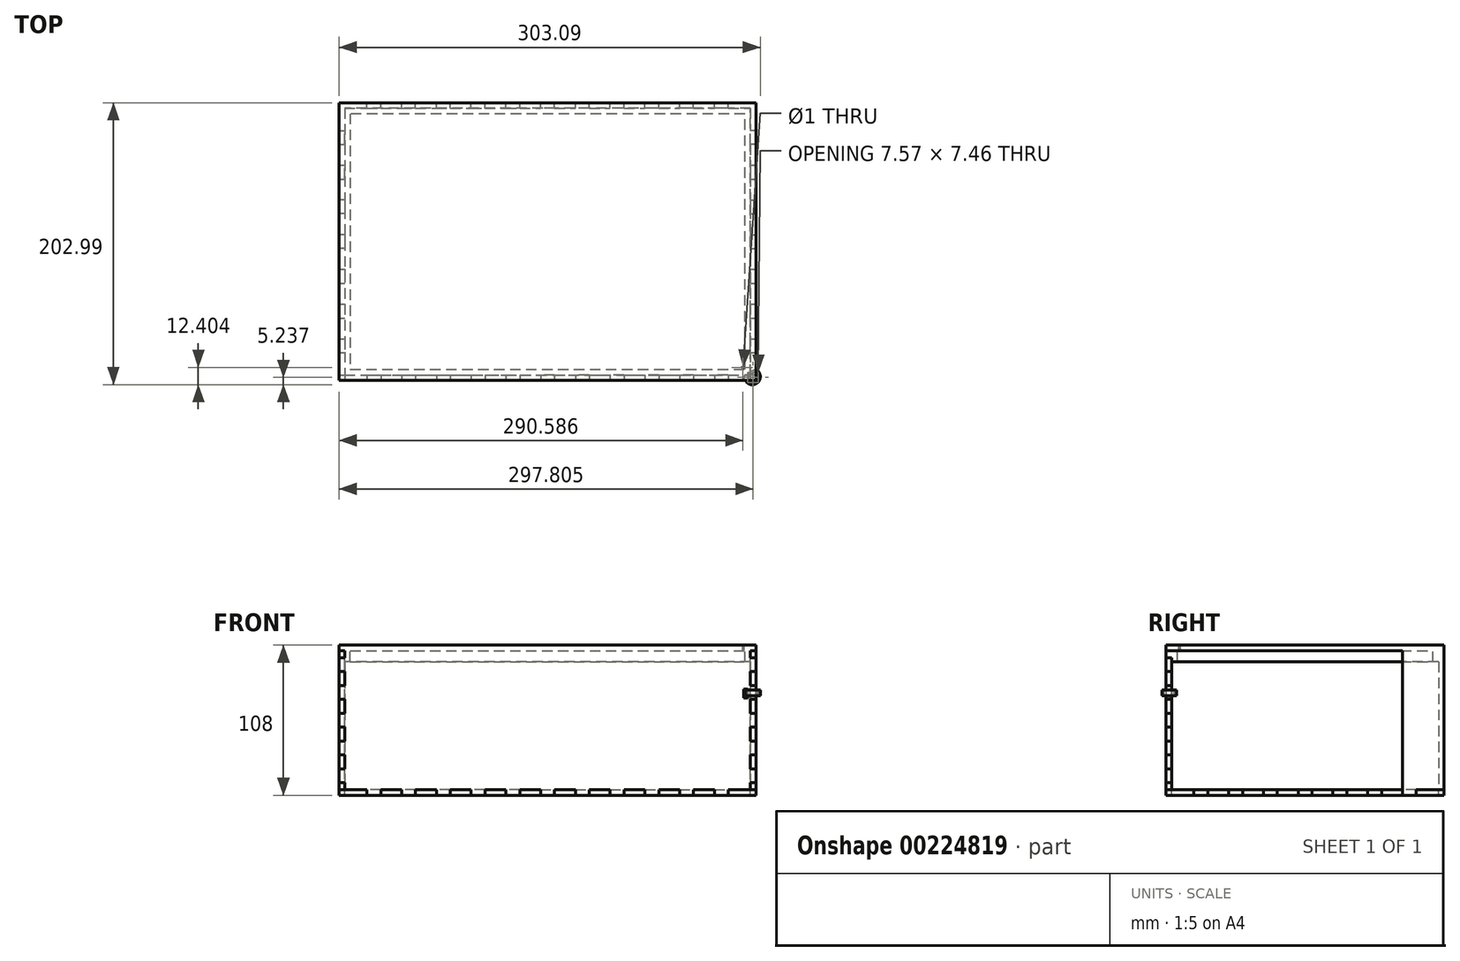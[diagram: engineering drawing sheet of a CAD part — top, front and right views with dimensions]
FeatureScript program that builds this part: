
annotation { "Feature Type Name" : "Feature", "Feature Type Description" : "" }
export const myFeature = defineFeature(function(context is Context, id is Id, definition is map)
    precondition{}
    {
        {
            var Q0;
            Q0=qCreatedBy(makeId("Top.planeOp"),FACE);
            var sketch = newSketch(context, id + "F0", { "sketchPlane" : qUnion([Q0])});
            skPoint(sketch, "E0.middle", {"position": v(0, 0) * mm});
            skLineSegment(sketch, "E1", {"start": v(-150, 0) * mm, "end": v(-150, 0) * mm, "construction": true});
            skPoint(sketch, "E1.endSnap0", {"position": v(-150, 0) * mm});
            skLineSegment(sketch, "E2", {"start": v(-146, 5) * mm, "end": v(-150, 5) * mm});
            skLineSegment(sketch, "E3.MirrorCS", {"start": v(-146, -5) * mm, "end": v(-150, -5) * mm});
            skLineSegment(sketch, "E4", {"start": v(-146, 5) * mm, "end": v(-146, -5) * mm});
            skLineSegment(sketch, "E5", {"start": v(-150, 0) * mm, "end": v(-83.06, 0) * mm, "construction": true});
            skLineSegment(sketch, "E6.0.1.0", {"start": v(-146, 30) * mm, "end": v(-150, 30) * mm});
            skLineSegment(sketch, "E6.0.1.1", {"start": v(-146, 30) * mm, "end": v(-146, 20) * mm});
            skLineSegment(sketch, "E6.0.1.2", {"start": v(-146, 20) * mm, "end": v(-150, 20) * mm});
            skLineSegment(sketch, "E6.0.2.0", {"start": v(-146, 55) * mm, "end": v(-150, 55) * mm});
            skLineSegment(sketch, "E6.0.2.1", {"start": v(-146, 55) * mm, "end": v(-146, 45) * mm});
            skLineSegment(sketch, "E6.0.2.2", {"start": v(-146, 45) * mm, "end": v(-150, 45) * mm});
            skLineSegment(sketch, "E6.0.3.0", {"start": v(-146, 80) * mm, "end": v(-150, 80) * mm});
            skLineSegment(sketch, "E6.0.3.1", {"start": v(-146, 80) * mm, "end": v(-146, 70) * mm});
            skLineSegment(sketch, "E6.0.3.2", {"start": v(-146, 70) * mm, "end": v(-150, 70) * mm});
            skLineSegment(sketch, "E6.direction1", {"start": v(-150, 5) * mm, "end": v(-128.8, 5.3) * mm, "construction": true});
            skLineSegment(sketch, "E6.direction2", {"start": v(-150, 5) * mm, "end": v(-150, 30) * mm, "construction": true});
            skLineSegment(sketch, "E7.MirrorCS", {"start": v(-146, -30) * mm, "end": v(-150, -30) * mm});
            skLineSegment(sketch, "E8.MirrorCS", {"start": v(-146, -55) * mm, "end": v(-150, -55) * mm});
            skLineSegment(sketch, "E9.MirrorCS", {"start": v(-146, -20) * mm, "end": v(-150, -20) * mm});
            skLineSegment(sketch, "E10.MirrorCS", {"start": v(-146, -45) * mm, "end": v(-150, -45) * mm});
            skLineSegment(sketch, "E11.MirrorCS", {"start": v(-146, -80) * mm, "end": v(-150, -80) * mm});
            skLineSegment(sketch, "E12.MirrorCS", {"start": v(-146, -70) * mm, "end": v(-150, -70) * mm});
            skLineSegment(sketch, "E13.MirrorCS", {"start": v(-146, -80) * mm, "end": v(-146, -70) * mm});
            skLineSegment(sketch, "E14.MirrorCS", {"start": v(-146, -30) * mm, "end": v(-146, -20) * mm});
            skLineSegment(sketch, "E15.MirrorCS", {"start": v(-146, -55) * mm, "end": v(-146, -45) * mm});
            skLineSegment(sketch, "E16.MirrorCS", {"start": v(-150, -5) * mm, "end": v(-150, -30) * mm, "construction": true});
            skLineSegment(sketch, "E17", {"start": v(-150, 100) * mm, "end": v(-150, 80) * mm});
            skLineSegment(sketch, "E18", {"start": v(-150, 70) * mm, "end": v(-150, 55) * mm});
            skLineSegment(sketch, "E19", {"start": v(-150, 45) * mm, "end": v(-150, 30) * mm});
            skLineSegment(sketch, "E20", {"start": v(-150, 20) * mm, "end": v(-150, 5) * mm});
            skLineSegment(sketch, "E21", {"start": v(-150, -5) * mm, "end": v(-150, -20) * mm});
            skLineSegment(sketch, "E22", {"start": v(-150, -30) * mm, "end": v(-150, -45) * mm});
            skLineSegment(sketch, "E23", {"start": v(-150, -55) * mm, "end": v(-150, -70) * mm});
            skLineSegment(sketch, "E24", {"start": v(-150, -80) * mm, "end": v(-150, -100) * mm});
            skLineSegment(sketch, "E25.MirrorCS", {"start": v(150, 0) * mm, "end": v(150, 0) * mm, "construction": true});
            skLineSegment(sketch, "E26.MirrorCS", {"start": v(146, -5) * mm, "end": v(150, -5) * mm});
            skLineSegment(sketch, "E27.MirrorCS", {"start": v(146, 5) * mm, "end": v(150, 5) * mm});
            skLineSegment(sketch, "E28.MirrorCS", {"start": v(146, -55) * mm, "end": v(150, -55) * mm});
            skLineSegment(sketch, "E29.MirrorCS", {"start": v(146, -20) * mm, "end": v(150, -20) * mm});
            skLineSegment(sketch, "E30.MirrorCS", {"start": v(146, 5) * mm, "end": v(146, -5) * mm});
            skLineSegment(sketch, "E31.MirrorCS", {"start": v(146, 70) * mm, "end": v(150, 70) * mm});
            skLineSegment(sketch, "E32.MirrorCS", {"start": v(146, 30) * mm, "end": v(150, 30) * mm});
            skLineSegment(sketch, "E33.MirrorCS", {"start": v(146, -30) * mm, "end": v(150, -30) * mm});
            skLineSegment(sketch, "E34.MirrorCS", {"start": v(146, 20) * mm, "end": v(150, 20) * mm});
            skLineSegment(sketch, "E35.MirrorCS", {"start": v(146, -45) * mm, "end": v(150, -45) * mm});
            skLineSegment(sketch, "E36.MirrorCS", {"start": v(146, -70) * mm, "end": v(150, -70) * mm});
            skLineSegment(sketch, "E37.MirrorCS", {"start": v(146, 55) * mm, "end": v(150, 55) * mm});
            skLineSegment(sketch, "E38.MirrorCS", {"start": v(146, -80) * mm, "end": v(150, -80) * mm});
            skLineSegment(sketch, "E39.MirrorCS", {"start": v(146, 45) * mm, "end": v(150, 45) * mm});
            skLineSegment(sketch, "E40.MirrorCS", {"start": v(146, 80) * mm, "end": v(150, 80) * mm});
            skLineSegment(sketch, "E41.MirrorCS", {"start": v(150, -5) * mm, "end": v(150, -20) * mm});
            skPoint(sketch, "E42.MirrorP", {"position": v(150, 0) * mm});
            skLineSegment(sketch, "E43.MirrorCS", {"start": v(150, 20) * mm, "end": v(150, 5) * mm});
            skLineSegment(sketch, "E44.MirrorCS", {"start": v(150, 70) * mm, "end": v(150, 55) * mm});
            skLineSegment(sketch, "E45.MirrorCS", {"start": v(146, 30) * mm, "end": v(146, 20) * mm});
            skLineSegment(sketch, "E46.MirrorCS", {"start": v(146, 55) * mm, "end": v(146, 45) * mm});
            skLineSegment(sketch, "E47.MirrorCS", {"start": v(146, -30) * mm, "end": v(146, -20) * mm});
            skLineSegment(sketch, "E48.MirrorCS", {"start": v(150, -55) * mm, "end": v(150, -70) * mm});
            skLineSegment(sketch, "E49.MirrorCS", {"start": v(150, 45) * mm, "end": v(150, 30) * mm});
            skLineSegment(sketch, "E50.MirrorCS", {"start": v(150, -30) * mm, "end": v(150, -45) * mm});
            skLineSegment(sketch, "E51.MirrorCS", {"start": v(146, -80) * mm, "end": v(146, -70) * mm});
            skLineSegment(sketch, "E52.MirrorCS", {"start": v(146, -55) * mm, "end": v(146, -45) * mm});
            skLineSegment(sketch, "E53.MirrorCS", {"start": v(146, 80) * mm, "end": v(146, 70) * mm});
            skLineSegment(sketch, "E54", {"start": v(150, 100) * mm, "end": v(150, 80) * mm});
            skLineSegment(sketch, "E55", {"start": v(150, -100) * mm, "end": v(150, -80) * mm});
            skLineSegment(sketch, "E56", {"start": v(0, 100) * mm, "end": v(0, 96) * mm, "construction": true});
            skLineSegment(sketch, "E57", {"start": v(0, 96) * mm, "end": v(5, 96) * mm, "construction": true});
            skLineSegment(sketch, "E58", {"start": v(5, 96) * mm, "end": v(5, 100) * mm});
            skLineSegment(sketch, "E59.MirrorCS", {"start": v(-5, 96) * mm, "end": v(-5, 100) * mm});
            skLineSegment(sketch, "E60", {"start": v(-5, 96) * mm, "end": v(5, 96) * mm});
            skLineSegment(sketch, "E61.1.0.0", {"start": v(20, 96) * mm, "end": v(20, 100) * mm});
            skLineSegment(sketch, "E61.1.0.1", {"start": v(30, 96) * mm, "end": v(30, 100) * mm});
            skLineSegment(sketch, "E61.1.0.2", {"start": v(20, 96) * mm, "end": v(30, 96) * mm});
            skLineSegment(sketch, "E61.2.0.0", {"start": v(45, 96) * mm, "end": v(45, 100) * mm});
            skLineSegment(sketch, "E61.2.0.1", {"start": v(55, 96) * mm, "end": v(55, 100) * mm});
            skLineSegment(sketch, "E61.2.0.2", {"start": v(45, 96) * mm, "end": v(55, 96) * mm});
            skLineSegment(sketch, "E61.3.0.0", {"start": v(70, 96) * mm, "end": v(70, 100) * mm});
            skLineSegment(sketch, "E61.3.0.1", {"start": v(80, 96) * mm, "end": v(80, 100) * mm});
            skLineSegment(sketch, "E61.3.0.2", {"start": v(70, 96) * mm, "end": v(80, 96) * mm});
            skLineSegment(sketch, "E61.4.0.0", {"start": v(95, 96) * mm, "end": v(95, 100) * mm});
            skLineSegment(sketch, "E61.4.0.1", {"start": v(105, 96) * mm, "end": v(105, 100) * mm});
            skLineSegment(sketch, "E61.4.0.2", {"start": v(95, 96) * mm, "end": v(105, 96) * mm});
            skLineSegment(sketch, "E61.5.0.0", {"start": v(120, 96) * mm, "end": v(120, 100) * mm});
            skLineSegment(sketch, "E61.5.0.1", {"start": v(130, 96) * mm, "end": v(130, 100) * mm});
            skLineSegment(sketch, "E61.5.0.2", {"start": v(120, 96) * mm, "end": v(130, 96) * mm});
            skLineSegment(sketch, "E61.direction1", {"start": v(-5, 96) * mm, "end": v(20, 96) * mm, "construction": true});
            skLineSegment(sketch, "E62.MirrorCS", {"start": v(5, 96) * mm, "end": v(-5, 96) * mm});
            skLineSegment(sketch, "E63.MirrorCS", {"start": v(0, 96) * mm, "end": v(-5, 96) * mm, "construction": true});
            skLineSegment(sketch, "E64.MirrorCS", {"start": v(-95, 96) * mm, "end": v(-95, 100) * mm});
            skLineSegment(sketch, "E65.MirrorCS", {"start": v(-20, 96) * mm, "end": v(-20, 100) * mm});
            skLineSegment(sketch, "E66.MirrorCS", {"start": v(-120, 96) * mm, "end": v(-120, 100) * mm});
            skLineSegment(sketch, "E67.MirrorCS", {"start": v(-105, 96) * mm, "end": v(-105, 100) * mm});
            skLineSegment(sketch, "E68.MirrorCS", {"start": v(-45, 96) * mm, "end": v(-45, 100) * mm});
            skLineSegment(sketch, "E69.MirrorCS", {"start": v(-30, 96) * mm, "end": v(-30, 100) * mm});
            skLineSegment(sketch, "E70.MirrorCS", {"start": v(-80, 96) * mm, "end": v(-80, 100) * mm});
            skLineSegment(sketch, "E71.MirrorCS", {"start": v(-55, 96) * mm, "end": v(-55, 100) * mm});
            skLineSegment(sketch, "E72.MirrorCS", {"start": v(-70, 96) * mm, "end": v(-70, 100) * mm});
            skLineSegment(sketch, "E73.MirrorCS", {"start": v(-130, 96) * mm, "end": v(-130, 100) * mm});
            skLineSegment(sketch, "E74.MirrorCS", {"start": v(-70, 96) * mm, "end": v(-80, 96) * mm});
            skLineSegment(sketch, "E75.MirrorCS", {"start": v(5, 96) * mm, "end": v(-20, 96) * mm, "construction": true});
            skLineSegment(sketch, "E76.MirrorCS", {"start": v(-45, 96) * mm, "end": v(-55, 96) * mm});
            skLineSegment(sketch, "E77.MirrorCS", {"start": v(-95, 96) * mm, "end": v(-105, 96) * mm});
            skLineSegment(sketch, "E78.MirrorCS", {"start": v(-20, 96) * mm, "end": v(-30, 96) * mm});
            skLineSegment(sketch, "E79.MirrorCS", {"start": v(-120, 96) * mm, "end": v(-130, 96) * mm});
            skLineSegment(sketch, "E80", {"start": v(-150, 100) * mm, "end": v(-130, 100) * mm});
            skLineSegment(sketch, "E81", {"start": v(-120, 100) * mm, "end": v(-105, 100) * mm});
            skLineSegment(sketch, "E82", {"start": v(-95, 100) * mm, "end": v(-80, 100) * mm});
            skLineSegment(sketch, "E83", {"start": v(-70, 100) * mm, "end": v(-55, 100) * mm});
            skLineSegment(sketch, "E84", {"start": v(-45, 100) * mm, "end": v(-30, 100) * mm});
            skLineSegment(sketch, "E85", {"start": v(-20, 100) * mm, "end": v(-5, 100) * mm});
            skLineSegment(sketch, "E86", {"start": v(5, 100) * mm, "end": v(20, 100) * mm});
            skLineSegment(sketch, "E87", {"start": v(30, 100) * mm, "end": v(45, 100) * mm});
            skLineSegment(sketch, "E88", {"start": v(55, 100) * mm, "end": v(70, 100) * mm});
            skLineSegment(sketch, "E89", {"start": v(80, 100) * mm, "end": v(95, 100) * mm});
            skLineSegment(sketch, "E90", {"start": v(105, 100) * mm, "end": v(120, 100) * mm});
            skLineSegment(sketch, "E91", {"start": v(130, 100) * mm, "end": v(150, 100) * mm});
            skLineSegment(sketch, "E92.MirrorCS", {"start": v(-5, -96) * mm, "end": v(5, -96) * mm});
            skLineSegment(sketch, "E93.MirrorCS", {"start": v(5, -96) * mm, "end": v(-5, -96) * mm});
            skLineSegment(sketch, "E94.MirrorCS", {"start": v(-5, -96) * mm, "end": v(-5, -100) * mm});
            skLineSegment(sketch, "E95.MirrorCS", {"start": v(5, -96) * mm, "end": v(5, -100) * mm});
            skLineSegment(sketch, "E96.MirrorCS", {"start": v(0, -96) * mm, "end": v(5, -96) * mm, "construction": true});
            skLineSegment(sketch, "E97.MirrorCS", {"start": v(0, -96) * mm, "end": v(-5, -96) * mm, "construction": true});
            skLineSegment(sketch, "E98.MirrorCS", {"start": v(-55, -96) * mm, "end": v(-55, -100) * mm});
            skLineSegment(sketch, "E99.MirrorCS", {"start": v(45, -96) * mm, "end": v(45, -100) * mm});
            skLineSegment(sketch, "E100.MirrorCS", {"start": v(-20, -96) * mm, "end": v(-20, -100) * mm});
            skLineSegment(sketch, "E101.MirrorCS", {"start": v(120, -96) * mm, "end": v(120, -100) * mm});
            skLineSegment(sketch, "E102.MirrorCS", {"start": v(-105, -96) * mm, "end": v(-105, -100) * mm});
            skLineSegment(sketch, "E103.MirrorCS", {"start": v(105, -96) * mm, "end": v(105, -100) * mm});
            skLineSegment(sketch, "E104.MirrorCS", {"start": v(30, -96) * mm, "end": v(30, -100) * mm});
            skLineSegment(sketch, "E105.MirrorCS", {"start": v(20, -96) * mm, "end": v(20, -100) * mm});
            skLineSegment(sketch, "E106.MirrorCS", {"start": v(130, -96) * mm, "end": v(130, -100) * mm});
            skLineSegment(sketch, "E107.MirrorCS", {"start": v(-80, -96) * mm, "end": v(-80, -100) * mm});
            skLineSegment(sketch, "E108.MirrorCS", {"start": v(80, -96) * mm, "end": v(80, -100) * mm});
            skLineSegment(sketch, "E109.MirrorCS", {"start": v(-130, -96) * mm, "end": v(-130, -100) * mm});
            skLineSegment(sketch, "E110.MirrorCS", {"start": v(-120, -96) * mm, "end": v(-120, -100) * mm});
            skLineSegment(sketch, "E111.MirrorCS", {"start": v(95, -96) * mm, "end": v(95, -100) * mm});
            skLineSegment(sketch, "E112.MirrorCS", {"start": v(-70, -96) * mm, "end": v(-70, -100) * mm});
            skLineSegment(sketch, "E113.MirrorCS", {"start": v(-95, -96) * mm, "end": v(-95, -100) * mm});
            skLineSegment(sketch, "E114.MirrorCS", {"start": v(55, -96) * mm, "end": v(55, -100) * mm});
            skLineSegment(sketch, "E115.MirrorCS", {"start": v(70, -96) * mm, "end": v(70, -100) * mm});
            skLineSegment(sketch, "E116.MirrorCS", {"start": v(-45, -96) * mm, "end": v(-45, -100) * mm});
            skLineSegment(sketch, "E117.MirrorCS", {"start": v(-30, -96) * mm, "end": v(-30, -100) * mm});
            skLineSegment(sketch, "E118.MirrorCS", {"start": v(0, -100) * mm, "end": v(0, -96) * mm, "construction": true});
            skLineSegment(sketch, "E119.MirrorCS", {"start": v(5, -100) * mm, "end": v(20, -100) * mm});
            skLineSegment(sketch, "E120.MirrorCS", {"start": v(30, -100) * mm, "end": v(45, -100) * mm});
            skLineSegment(sketch, "E121.MirrorCS", {"start": v(-120, -96) * mm, "end": v(-130, -96) * mm});
            skLineSegment(sketch, "E122.MirrorCS", {"start": v(45, -96) * mm, "end": v(55, -96) * mm});
            skLineSegment(sketch, "E123.MirrorCS", {"start": v(-120, -100) * mm, "end": v(-105, -100) * mm});
            skLineSegment(sketch, "E124.MirrorCS", {"start": v(-95, -96) * mm, "end": v(-105, -96) * mm});
            skLineSegment(sketch, "E125.MirrorCS", {"start": v(-20, -100) * mm, "end": v(-5, -100) * mm});
            skLineSegment(sketch, "E126.MirrorCS", {"start": v(-45, -96) * mm, "end": v(-55, -96) * mm});
            skLineSegment(sketch, "E127.MirrorCS", {"start": v(-20, -96) * mm, "end": v(-30, -96) * mm});
            skLineSegment(sketch, "E128.MirrorCS", {"start": v(20, -96) * mm, "end": v(30, -96) * mm});
            skLineSegment(sketch, "E129.MirrorCS", {"start": v(105, -100) * mm, "end": v(120, -100) * mm});
            skLineSegment(sketch, "E130.MirrorCS", {"start": v(-150, -100) * mm, "end": v(-130, -100) * mm});
            skLineSegment(sketch, "E131.MirrorCS", {"start": v(55, -100) * mm, "end": v(70, -100) * mm});
            skLineSegment(sketch, "E132.MirrorCS", {"start": v(-45, -100) * mm, "end": v(-30, -100) * mm});
            skLineSegment(sketch, "E133.MirrorCS", {"start": v(5, -96) * mm, "end": v(-20, -96) * mm, "construction": true});
            skLineSegment(sketch, "E134.MirrorCS", {"start": v(-5, -96) * mm, "end": v(20, -96) * mm, "construction": true});
            skLineSegment(sketch, "E135.MirrorCS", {"start": v(-95, -100) * mm, "end": v(-80, -100) * mm});
            skLineSegment(sketch, "E136.MirrorCS", {"start": v(130, -100) * mm, "end": v(150, -100) * mm});
            skLineSegment(sketch, "E137.MirrorCS", {"start": v(70, -96) * mm, "end": v(80, -96) * mm});
            skLineSegment(sketch, "E138.MirrorCS", {"start": v(120, -96) * mm, "end": v(130, -96) * mm});
            skLineSegment(sketch, "E139.MirrorCS", {"start": v(-70, -96) * mm, "end": v(-80, -96) * mm});
            skLineSegment(sketch, "E140.MirrorCS", {"start": v(80, -100) * mm, "end": v(95, -100) * mm});
            skLineSegment(sketch, "E141.MirrorCS", {"start": v(-70, -100) * mm, "end": v(-55, -100) * mm});
            skLineSegment(sketch, "E142.MirrorCS", {"start": v(95, -96) * mm, "end": v(105, -96) * mm});
            skSolve(sketch);
        }
        {
            var Q0;
            Q0=makeQuery(id+"F0.imprint","IMPRINT",FACE,{"disambiguationData":[TD([[makeQuery(id+"F0.imprint","IMPRINT",EDGE,{"derivedFrom":sQuery(id+"F0.wireOp",EDGE,"E2")}),-1.0]])]});
            extrude(context, id + "F1", {"entities" : qUnion([Q0]), "depth" : 4 * mm});
        }
        {
            var Q0;
            Q0=makeQuery(id+"F1.opExtrude","CAP_FACE",FACE,{"disambiguationData":[OSD([sQuery(id+"F0.wireOp",EDGE,"E2"),sQuery(id+"F0.wireOp",EDGE,"E4"),sQuery(id+"F0.wireOp",EDGE,"E6.0.1.0"),sQuery(id+"F0.wireOp",EDGE,"E6.0.1.1"),sQuery(id+"F0.wireOp",EDGE,"E6.0.1.2"),sQuery(id+"F0.wireOp",EDGE,"E6.0.2.0"),sQuery(id+"F0.wireOp",EDGE,"E6.0.2.1"),sQuery(id+"F0.wireOp",EDGE,"E6.0.2.2"),sQuery(id+"F0.wireOp",EDGE,"E6.0.3.0"),sQuery(id+"F0.wireOp",EDGE,"E6.0.3.1"),sQuery(id+"F0.wireOp",EDGE,"E6.0.3.2"),sQuery(id+"F0.wireOp",EDGE,"E7.MirrorCS"),sQuery(id+"F0.wireOp",EDGE,"E3.MirrorCS"),sQuery(id+"F0.wireOp",EDGE,"E8.MirrorCS"),sQuery(id+"F0.wireOp",EDGE,"E9.MirrorCS"),sQuery(id+"F0.wireOp",EDGE,"E10.MirrorCS"),sQuery(id+"F0.wireOp",EDGE,"E11.MirrorCS"),sQuery(id+"F0.wireOp",EDGE,"E12.MirrorCS"),sQuery(id+"F0.wireOp",EDGE,"E13.MirrorCS"),sQuery(id+"F0.wireOp",EDGE,"E14.MirrorCS"),sQuery(id+"F0.wireOp",EDGE,"E15.MirrorCS"),sQuery(id+"F0.wireOp",EDGE,"E17"),sQuery(id+"F0.wireOp",EDGE,"E18"),sQuery(id+"F0.wireOp",EDGE,"E19"),sQuery(id+"F0.wireOp",EDGE,"E20"),sQuery(id+"F0.wireOp",EDGE,"E21"),sQuery(id+"F0.wireOp",EDGE,"E22"),sQuery(id+"F0.wireOp",EDGE,"E23"),sQuery(id+"F0.wireOp",EDGE,"E24"),sQuery(id+"F0.wireOp",EDGE,"E27.MirrorCS"),sQuery(id+"F0.wireOp",EDGE,"E26.MirrorCS"),sQuery(id+"F0.wireOp",EDGE,"E28.MirrorCS"),sQuery(id+"F0.wireOp",EDGE,"E29.MirrorCS"),sQuery(id+"F0.wireOp",EDGE,"E30.MirrorCS"),sQuery(id+"F0.wireOp",EDGE,"E31.MirrorCS"),sQuery(id+"F0.wireOp",EDGE,"E32.MirrorCS"),sQuery(id+"F0.wireOp",EDGE,"E33.MirrorCS"),sQuery(id+"F0.wireOp",EDGE,"E34.MirrorCS"),sQuery(id+"F0.wireOp",EDGE,"E35.MirrorCS"),sQuery(id+"F0.wireOp",EDGE,"E36.MirrorCS"),sQuery(id+"F0.wireOp",EDGE,"E37.MirrorCS"),sQuery(id+"F0.wireOp",EDGE,"E38.MirrorCS"),sQuery(id+"F0.wireOp",EDGE,"E39.MirrorCS"),sQuery(id+"F0.wireOp",EDGE,"E40.MirrorCS"),sQuery(id+"F0.wireOp",EDGE,"E41.MirrorCS"),sQuery(id+"F0.wireOp",EDGE,"E43.MirrorCS"),sQuery(id+"F0.wireOp",EDGE,"E44.MirrorCS"),sQuery(id+"F0.wireOp",EDGE,"E45.MirrorCS"),sQuery(id+"F0.wireOp",EDGE,"E46.MirrorCS"),sQuery(id+"F0.wireOp",EDGE,"E47.MirrorCS"),sQuery(id+"F0.wireOp",EDGE,"E48.MirrorCS"),sQuery(id+"F0.wireOp",EDGE,"E49.MirrorCS"),sQuery(id+"F0.wireOp",EDGE,"E50.MirrorCS"),sQuery(id+"F0.wireOp",EDGE,"E51.MirrorCS"),sQuery(id+"F0.wireOp",EDGE,"E52.MirrorCS"),sQuery(id+"F0.wireOp",EDGE,"E53.MirrorCS"),sQuery(id+"F0.wireOp",EDGE,"E54"),sQuery(id+"F0.wireOp",EDGE,"E55"),sQuery(id+"F0.wireOp",EDGE,"E61.1.0.0"),sQuery(id+"F0.wireOp",EDGE,"E61.1.0.1"),sQuery(id+"F0.wireOp",EDGE,"E61.1.0.2"),sQuery(id+"F0.wireOp",EDGE,"E61.2.0.0"),sQuery(id+"F0.wireOp",EDGE,"E61.2.0.1"),sQuery(id+"F0.wireOp",EDGE,"E61.2.0.2"),sQuery(id+"F0.wireOp",EDGE,"E61.3.0.0"),sQuery(id+"F0.wireOp",EDGE,"E61.3.0.1"),sQuery(id+"F0.wireOp",EDGE,"E61.3.0.2"),sQuery(id+"F0.wireOp",EDGE,"E61.4.0.0"),sQuery(id+"F0.wireOp",EDGE,"E61.4.0.1"),sQuery(id+"F0.wireOp",EDGE,"E61.4.0.2"),sQuery(id+"F0.wireOp",EDGE,"E61.5.0.0"),sQuery(id+"F0.wireOp",EDGE,"E61.5.0.1"),sQuery(id+"F0.wireOp",EDGE,"E61.5.0.2"),sQuery(id+"F0.wireOp",EDGE,"E62.MirrorCS"),sQuery(id+"F0.wireOp",EDGE,"E64.MirrorCS"),sQuery(id+"F0.wireOp",EDGE,"E65.MirrorCS"),sQuery(id+"F0.wireOp",EDGE,"E66.MirrorCS"),sQuery(id+"F0.wireOp",EDGE,"E67.MirrorCS"),sQuery(id+"F0.wireOp",EDGE,"E68.MirrorCS"),sQuery(id+"F0.wireOp",EDGE,"E69.MirrorCS"),sQuery(id+"F0.wireOp",EDGE,"E70.MirrorCS"),sQuery(id+"F0.wireOp",EDGE,"E59.MirrorCS"),sQuery(id+"F0.wireOp",EDGE,"E58"),sQuery(id+"F0.wireOp",EDGE,"E71.MirrorCS"),sQuery(id+"F0.wireOp",EDGE,"E72.MirrorCS"),sQuery(id+"F0.wireOp",EDGE,"E73.MirrorCS"),sQuery(id+"F0.wireOp",EDGE,"E74.MirrorCS"),sQuery(id+"F0.wireOp",EDGE,"E76.MirrorCS"),sQuery(id+"F0.wireOp",EDGE,"E77.MirrorCS"),sQuery(id+"F0.wireOp",EDGE,"E78.MirrorCS"),sQuery(id+"F0.wireOp",EDGE,"E79.MirrorCS"),sQuery(id+"F0.wireOp",EDGE,"E80"),sQuery(id+"F0.wireOp",EDGE,"E81"),sQuery(id+"F0.wireOp",EDGE,"E82"),sQuery(id+"F0.wireOp",EDGE,"E83"),sQuery(id+"F0.wireOp",EDGE,"E84"),sQuery(id+"F0.wireOp",EDGE,"E85"),sQuery(id+"F0.wireOp",EDGE,"E86"),sQuery(id+"F0.wireOp",EDGE,"E87"),sQuery(id+"F0.wireOp",EDGE,"E88"),sQuery(id+"F0.wireOp",EDGE,"E89"),sQuery(id+"F0.wireOp",EDGE,"E90"),sQuery(id+"F0.wireOp",EDGE,"E91"),sQuery(id+"F0.wireOp",EDGE,"E93.MirrorCS"),sQuery(id+"F0.wireOp",EDGE,"E95.MirrorCS"),sQuery(id+"F0.wireOp",EDGE,"E94.MirrorCS"),sQuery(id+"F0.wireOp",EDGE,"E98.MirrorCS"),sQuery(id+"F0.wireOp",EDGE,"E99.MirrorCS"),sQuery(id+"F0.wireOp",EDGE,"E100.MirrorCS"),sQuery(id+"F0.wireOp",EDGE,"E101.MirrorCS"),sQuery(id+"F0.wireOp",EDGE,"E102.MirrorCS"),sQuery(id+"F0.wireOp",EDGE,"E103.MirrorCS"),sQuery(id+"F0.wireOp",EDGE,"E104.MirrorCS"),sQuery(id+"F0.wireOp",EDGE,"E105.MirrorCS"),sQuery(id+"F0.wireOp",EDGE,"E106.MirrorCS"),sQuery(id+"F0.wireOp",EDGE,"E107.MirrorCS"),sQuery(id+"F0.wireOp",EDGE,"E108.MirrorCS"),sQuery(id+"F0.wireOp",EDGE,"E109.MirrorCS"),sQuery(id+"F0.wireOp",EDGE,"E110.MirrorCS"),sQuery(id+"F0.wireOp",EDGE,"E111.MirrorCS"),sQuery(id+"F0.wireOp",EDGE,"E112.MirrorCS"),sQuery(id+"F0.wireOp",EDGE,"E113.MirrorCS"),sQuery(id+"F0.wireOp",EDGE,"E114.MirrorCS"),sQuery(id+"F0.wireOp",EDGE,"E115.MirrorCS"),sQuery(id+"F0.wireOp",EDGE,"E116.MirrorCS"),sQuery(id+"F0.wireOp",EDGE,"E117.MirrorCS"),sQuery(id+"F0.wireOp",EDGE,"E119.MirrorCS"),sQuery(id+"F0.wireOp",EDGE,"E120.MirrorCS"),sQuery(id+"F0.wireOp",EDGE,"E121.MirrorCS"),sQuery(id+"F0.wireOp",EDGE,"E122.MirrorCS"),sQuery(id+"F0.wireOp",EDGE,"E123.MirrorCS"),sQuery(id+"F0.wireOp",EDGE,"E124.MirrorCS"),sQuery(id+"F0.wireOp",EDGE,"E125.MirrorCS"),sQuery(id+"F0.wireOp",EDGE,"E126.MirrorCS"),sQuery(id+"F0.wireOp",EDGE,"E127.MirrorCS"),sQuery(id+"F0.wireOp",EDGE,"E128.MirrorCS"),sQuery(id+"F0.wireOp",EDGE,"E129.MirrorCS"),sQuery(id+"F0.wireOp",EDGE,"E130.MirrorCS"),sQuery(id+"F0.wireOp",EDGE,"E131.MirrorCS"),sQuery(id+"F0.wireOp",EDGE,"E132.MirrorCS"),sQuery(id+"F0.wireOp",EDGE,"E135.MirrorCS"),sQuery(id+"F0.wireOp",EDGE,"E136.MirrorCS"),sQuery(id+"F0.wireOp",EDGE,"E137.MirrorCS"),sQuery(id+"F0.wireOp",EDGE,"E138.MirrorCS"),sQuery(id+"F0.wireOp",EDGE,"E139.MirrorCS"),sQuery(id+"F0.wireOp",EDGE,"E140.MirrorCS"),sQuery(id+"F0.wireOp",EDGE,"E141.MirrorCS"),sQuery(id+"F0.wireOp",EDGE,"E142.MirrorCS")])],"isStart":false});
            var sketch = newSketch(context, id + "F2", { "sketchPlane" : qUnion([Q0])});
            skLineSegment(sketch, "E143.0.58", {"start": v(-150, 80) * mm, "end": v(-146, 80) * mm});
            skLineSegment(sketch, "E143.0.59", {"start": v(-146, 80) * mm, "end": v(-146, 70) * mm});
            skLineSegment(sketch, "E143.0.60", {"start": v(-146, 70) * mm, "end": v(-150, 70) * mm});
            skLineSegment(sketch, "E143.0.61", {"start": v(-150, 70) * mm, "end": v(-150, 55) * mm});
            skLineSegment(sketch, "E143.0.62", {"start": v(-150, 55) * mm, "end": v(-146, 55) * mm});
            skLineSegment(sketch, "E143.0.63", {"start": v(-146, 55) * mm, "end": v(-146, 45) * mm});
            skLineSegment(sketch, "E143.0.64", {"start": v(-146, 45) * mm, "end": v(-150, 45) * mm});
            skLineSegment(sketch, "E143.0.65", {"start": v(-150, 45) * mm, "end": v(-150, 30) * mm});
            skLineSegment(sketch, "E143.0.66", {"start": v(-150, 30) * mm, "end": v(-146, 30) * mm});
            skLineSegment(sketch, "E143.0.67", {"start": v(-146, 30) * mm, "end": v(-146, 20) * mm});
            skLineSegment(sketch, "E143.0.68", {"start": v(-146, 20) * mm, "end": v(-150, 20) * mm});
            skLineSegment(sketch, "E143.0.69", {"start": v(-150, 20) * mm, "end": v(-150, 5) * mm});
            skLineSegment(sketch, "E143.0.70", {"start": v(-150, 5) * mm, "end": v(-146, 5) * mm});
            skLineSegment(sketch, "E143.0.71", {"start": v(-146, 5) * mm, "end": v(-146, -5) * mm});
            skLineSegment(sketch, "E143.0.72", {"start": v(-146, -5) * mm, "end": v(-150, -5) * mm});
            skLineSegment(sketch, "E143.0.73", {"start": v(-150, -5) * mm, "end": v(-150, -20) * mm});
            skLineSegment(sketch, "E143.0.74", {"start": v(-150, -20) * mm, "end": v(-146, -20) * mm});
            skLineSegment(sketch, "E143.0.75", {"start": v(-146, -20) * mm, "end": v(-146, -30) * mm});
            skLineSegment(sketch, "E143.0.76", {"start": v(-146, -30) * mm, "end": v(-150, -30) * mm});
            skLineSegment(sketch, "E143.0.77", {"start": v(-150, -30) * mm, "end": v(-150, -45) * mm});
            skLineSegment(sketch, "E143.0.78", {"start": v(-150, -45) * mm, "end": v(-146, -45) * mm});
            skLineSegment(sketch, "E143.0.79", {"start": v(-146, -45) * mm, "end": v(-146, -55) * mm});
            skLineSegment(sketch, "E143.0.80", {"start": v(-146, -55) * mm, "end": v(-150, -55) * mm});
            skLineSegment(sketch, "E143.0.81", {"start": v(-150, -55) * mm, "end": v(-150, -70) * mm});
            skLineSegment(sketch, "E143.0.82", {"start": v(-150, -70) * mm, "end": v(-146, -70) * mm});
            skLineSegment(sketch, "E143.0.83", {"start": v(-146, -70) * mm, "end": v(-146, -80) * mm});
            skLineSegment(sketch, "E143.0.84", {"start": v(-146, -80) * mm, "end": v(-150, -80) * mm});
            skLineSegment(sketch, "E144", {"start": v(-150, 80) * mm, "end": v(-150, 70) * mm});
            skLineSegment(sketch, "E145", {"start": v(-150, 55) * mm, "end": v(-150, 45) * mm});
            skLineSegment(sketch, "E146", {"start": v(-150, 30) * mm, "end": v(-150, 20) * mm});
            skLineSegment(sketch, "E147", {"start": v(-150, 5) * mm, "end": v(-150, -5) * mm});
            skLineSegment(sketch, "E148", {"start": v(-150, -20) * mm, "end": v(-150, -30) * mm});
            skLineSegment(sketch, "E149", {"start": v(-150, -45) * mm, "end": v(-150, -55) * mm});
            skLineSegment(sketch, "E150", {"start": v(-150, -70) * mm, "end": v(-150, -80) * mm});
            skSolve(sketch);
        }
        {
            var Q0;
            Q0=makeQuery(id+"F2.imprint","IMPRINT",FACE,{"disambiguationData":[TD([[makeQuery(id+"F2.imprint","IMPRINT",EDGE,{"derivedFrom":sQuery(id+"F2.wireOp",EDGE,"E143.0.58")}),1.0]])]});
            var Q1;
            Q1=makeQuery(id+"F2.imprint","IMPRINT",FACE,{"disambiguationData":[TD([[makeQuery(id+"F2.imprint","IMPRINT",EDGE,{"derivedFrom":sQuery(id+"F2.wireOp",EDGE,"E143.0.62")}),1.0]])]});
            var Q2;
            Q2=makeQuery(id+"F2.imprint","IMPRINT",FACE,{"disambiguationData":[TD([[makeQuery(id+"F2.imprint","IMPRINT",EDGE,{"derivedFrom":sQuery(id+"F2.wireOp",EDGE,"E143.0.66")}),1.0]])]});
            var Q3;
            Q3=makeQuery(id+"F2.imprint","IMPRINT",FACE,{"disambiguationData":[TD([[makeQuery(id+"F2.imprint","IMPRINT",EDGE,{"derivedFrom":sQuery(id+"F2.wireOp",EDGE,"E143.0.70")}),1.0]])]});
            var Q4;
            Q4=makeQuery(id+"F2.imprint","IMPRINT",FACE,{"disambiguationData":[TD([[makeQuery(id+"F2.imprint","IMPRINT",EDGE,{"derivedFrom":sQuery(id+"F2.wireOp",EDGE,"E143.0.74")}),1.0]])]});
            var Q5;
            Q5=makeQuery(id+"F2.imprint","IMPRINT",FACE,{"disambiguationData":[TD([[makeQuery(id+"F2.imprint","IMPRINT",EDGE,{"derivedFrom":sQuery(id+"F2.wireOp",EDGE,"E143.0.78")}),1.0]])]});
            var Q6;
            Q6=makeQuery(id+"F2.imprint","IMPRINT",FACE,{"disambiguationData":[TD([[makeQuery(id+"F2.imprint","IMPRINT",EDGE,{"derivedFrom":sQuery(id+"F2.wireOp",EDGE,"E143.0.82")}),1.0]])]});
            var Q7;
            Q7=makeQuery(id+"F1.opExtrude","CAP_FACE",FACE,{"disambiguationData":[OSD([sQuery(id+"F0.wireOp",EDGE,"E2"),sQuery(id+"F0.wireOp",EDGE,"E4"),sQuery(id+"F0.wireOp",EDGE,"E6.0.1.0"),sQuery(id+"F0.wireOp",EDGE,"E6.0.1.1"),sQuery(id+"F0.wireOp",EDGE,"E6.0.1.2"),sQuery(id+"F0.wireOp",EDGE,"E6.0.2.0"),sQuery(id+"F0.wireOp",EDGE,"E6.0.2.1"),sQuery(id+"F0.wireOp",EDGE,"E6.0.2.2"),sQuery(id+"F0.wireOp",EDGE,"E6.0.3.0"),sQuery(id+"F0.wireOp",EDGE,"E6.0.3.1"),sQuery(id+"F0.wireOp",EDGE,"E6.0.3.2"),sQuery(id+"F0.wireOp",EDGE,"E7.MirrorCS"),sQuery(id+"F0.wireOp",EDGE,"E3.MirrorCS"),sQuery(id+"F0.wireOp",EDGE,"E8.MirrorCS"),sQuery(id+"F0.wireOp",EDGE,"E9.MirrorCS"),sQuery(id+"F0.wireOp",EDGE,"E10.MirrorCS"),sQuery(id+"F0.wireOp",EDGE,"E11.MirrorCS"),sQuery(id+"F0.wireOp",EDGE,"E12.MirrorCS"),sQuery(id+"F0.wireOp",EDGE,"E13.MirrorCS"),sQuery(id+"F0.wireOp",EDGE,"E14.MirrorCS"),sQuery(id+"F0.wireOp",EDGE,"E15.MirrorCS"),sQuery(id+"F0.wireOp",EDGE,"E17"),sQuery(id+"F0.wireOp",EDGE,"E18"),sQuery(id+"F0.wireOp",EDGE,"E19"),sQuery(id+"F0.wireOp",EDGE,"E20"),sQuery(id+"F0.wireOp",EDGE,"E21"),sQuery(id+"F0.wireOp",EDGE,"E22"),sQuery(id+"F0.wireOp",EDGE,"E23"),sQuery(id+"F0.wireOp",EDGE,"E24"),sQuery(id+"F0.wireOp",EDGE,"E27.MirrorCS"),sQuery(id+"F0.wireOp",EDGE,"E26.MirrorCS"),sQuery(id+"F0.wireOp",EDGE,"E28.MirrorCS"),sQuery(id+"F0.wireOp",EDGE,"E29.MirrorCS"),sQuery(id+"F0.wireOp",EDGE,"E30.MirrorCS"),sQuery(id+"F0.wireOp",EDGE,"E31.MirrorCS"),sQuery(id+"F0.wireOp",EDGE,"E32.MirrorCS"),sQuery(id+"F0.wireOp",EDGE,"E33.MirrorCS"),sQuery(id+"F0.wireOp",EDGE,"E34.MirrorCS"),sQuery(id+"F0.wireOp",EDGE,"E35.MirrorCS"),sQuery(id+"F0.wireOp",EDGE,"E36.MirrorCS"),sQuery(id+"F0.wireOp",EDGE,"E37.MirrorCS"),sQuery(id+"F0.wireOp",EDGE,"E38.MirrorCS"),sQuery(id+"F0.wireOp",EDGE,"E39.MirrorCS"),sQuery(id+"F0.wireOp",EDGE,"E40.MirrorCS"),sQuery(id+"F0.wireOp",EDGE,"E41.MirrorCS"),sQuery(id+"F0.wireOp",EDGE,"E43.MirrorCS"),sQuery(id+"F0.wireOp",EDGE,"E44.MirrorCS"),sQuery(id+"F0.wireOp",EDGE,"E45.MirrorCS"),sQuery(id+"F0.wireOp",EDGE,"E46.MirrorCS"),sQuery(id+"F0.wireOp",EDGE,"E47.MirrorCS"),sQuery(id+"F0.wireOp",EDGE,"E48.MirrorCS"),sQuery(id+"F0.wireOp",EDGE,"E49.MirrorCS"),sQuery(id+"F0.wireOp",EDGE,"E50.MirrorCS"),sQuery(id+"F0.wireOp",EDGE,"E51.MirrorCS"),sQuery(id+"F0.wireOp",EDGE,"E52.MirrorCS"),sQuery(id+"F0.wireOp",EDGE,"E53.MirrorCS"),sQuery(id+"F0.wireOp",EDGE,"E54"),sQuery(id+"F0.wireOp",EDGE,"E55"),sQuery(id+"F0.wireOp",EDGE,"E61.1.0.0"),sQuery(id+"F0.wireOp",EDGE,"E61.1.0.1"),sQuery(id+"F0.wireOp",EDGE,"E61.1.0.2"),sQuery(id+"F0.wireOp",EDGE,"E61.2.0.0"),sQuery(id+"F0.wireOp",EDGE,"E61.2.0.1"),sQuery(id+"F0.wireOp",EDGE,"E61.2.0.2"),sQuery(id+"F0.wireOp",EDGE,"E61.3.0.0"),sQuery(id+"F0.wireOp",EDGE,"E61.3.0.1"),sQuery(id+"F0.wireOp",EDGE,"E61.3.0.2"),sQuery(id+"F0.wireOp",EDGE,"E61.4.0.0"),sQuery(id+"F0.wireOp",EDGE,"E61.4.0.1"),sQuery(id+"F0.wireOp",EDGE,"E61.4.0.2"),sQuery(id+"F0.wireOp",EDGE,"E61.5.0.0"),sQuery(id+"F0.wireOp",EDGE,"E61.5.0.1"),sQuery(id+"F0.wireOp",EDGE,"E61.5.0.2"),sQuery(id+"F0.wireOp",EDGE,"E62.MirrorCS"),sQuery(id+"F0.wireOp",EDGE,"E64.MirrorCS"),sQuery(id+"F0.wireOp",EDGE,"E65.MirrorCS"),sQuery(id+"F0.wireOp",EDGE,"E66.MirrorCS"),sQuery(id+"F0.wireOp",EDGE,"E67.MirrorCS"),sQuery(id+"F0.wireOp",EDGE,"E68.MirrorCS"),sQuery(id+"F0.wireOp",EDGE,"E69.MirrorCS"),sQuery(id+"F0.wireOp",EDGE,"E70.MirrorCS"),sQuery(id+"F0.wireOp",EDGE,"E59.MirrorCS"),sQuery(id+"F0.wireOp",EDGE,"E58"),sQuery(id+"F0.wireOp",EDGE,"E71.MirrorCS"),sQuery(id+"F0.wireOp",EDGE,"E72.MirrorCS"),sQuery(id+"F0.wireOp",EDGE,"E73.MirrorCS"),sQuery(id+"F0.wireOp",EDGE,"E74.MirrorCS"),sQuery(id+"F0.wireOp",EDGE,"E76.MirrorCS"),sQuery(id+"F0.wireOp",EDGE,"E77.MirrorCS"),sQuery(id+"F0.wireOp",EDGE,"E78.MirrorCS"),sQuery(id+"F0.wireOp",EDGE,"E79.MirrorCS"),sQuery(id+"F0.wireOp",EDGE,"E80"),sQuery(id+"F0.wireOp",EDGE,"E81"),sQuery(id+"F0.wireOp",EDGE,"E82"),sQuery(id+"F0.wireOp",EDGE,"E83"),sQuery(id+"F0.wireOp",EDGE,"E84"),sQuery(id+"F0.wireOp",EDGE,"E85"),sQuery(id+"F0.wireOp",EDGE,"E86"),sQuery(id+"F0.wireOp",EDGE,"E87"),sQuery(id+"F0.wireOp",EDGE,"E88"),sQuery(id+"F0.wireOp",EDGE,"E89"),sQuery(id+"F0.wireOp",EDGE,"E90"),sQuery(id+"F0.wireOp",EDGE,"E91"),sQuery(id+"F0.wireOp",EDGE,"E93.MirrorCS"),sQuery(id+"F0.wireOp",EDGE,"E95.MirrorCS"),sQuery(id+"F0.wireOp",EDGE,"E94.MirrorCS"),sQuery(id+"F0.wireOp",EDGE,"E98.MirrorCS"),sQuery(id+"F0.wireOp",EDGE,"E99.MirrorCS"),sQuery(id+"F0.wireOp",EDGE,"E100.MirrorCS"),sQuery(id+"F0.wireOp",EDGE,"E101.MirrorCS"),sQuery(id+"F0.wireOp",EDGE,"E102.MirrorCS"),sQuery(id+"F0.wireOp",EDGE,"E103.MirrorCS"),sQuery(id+"F0.wireOp",EDGE,"E104.MirrorCS"),sQuery(id+"F0.wireOp",EDGE,"E105.MirrorCS"),sQuery(id+"F0.wireOp",EDGE,"E106.MirrorCS"),sQuery(id+"F0.wireOp",EDGE,"E107.MirrorCS"),sQuery(id+"F0.wireOp",EDGE,"E108.MirrorCS"),sQuery(id+"F0.wireOp",EDGE,"E109.MirrorCS"),sQuery(id+"F0.wireOp",EDGE,"E110.MirrorCS"),sQuery(id+"F0.wireOp",EDGE,"E111.MirrorCS"),sQuery(id+"F0.wireOp",EDGE,"E112.MirrorCS"),sQuery(id+"F0.wireOp",EDGE,"E113.MirrorCS"),sQuery(id+"F0.wireOp",EDGE,"E114.MirrorCS"),sQuery(id+"F0.wireOp",EDGE,"E115.MirrorCS"),sQuery(id+"F0.wireOp",EDGE,"E116.MirrorCS"),sQuery(id+"F0.wireOp",EDGE,"E117.MirrorCS"),sQuery(id+"F0.wireOp",EDGE,"E119.MirrorCS"),sQuery(id+"F0.wireOp",EDGE,"E120.MirrorCS"),sQuery(id+"F0.wireOp",EDGE,"E121.MirrorCS"),sQuery(id+"F0.wireOp",EDGE,"E122.MirrorCS"),sQuery(id+"F0.wireOp",EDGE,"E123.MirrorCS"),sQuery(id+"F0.wireOp",EDGE,"E124.MirrorCS"),sQuery(id+"F0.wireOp",EDGE,"E125.MirrorCS"),sQuery(id+"F0.wireOp",EDGE,"E126.MirrorCS"),sQuery(id+"F0.wireOp",EDGE,"E127.MirrorCS"),sQuery(id+"F0.wireOp",EDGE,"E128.MirrorCS"),sQuery(id+"F0.wireOp",EDGE,"E129.MirrorCS"),sQuery(id+"F0.wireOp",EDGE,"E130.MirrorCS"),sQuery(id+"F0.wireOp",EDGE,"E131.MirrorCS"),sQuery(id+"F0.wireOp",EDGE,"E132.MirrorCS"),sQuery(id+"F0.wireOp",EDGE,"E135.MirrorCS"),sQuery(id+"F0.wireOp",EDGE,"E136.MirrorCS"),sQuery(id+"F0.wireOp",EDGE,"E137.MirrorCS"),sQuery(id+"F0.wireOp",EDGE,"E138.MirrorCS"),sQuery(id+"F0.wireOp",EDGE,"E139.MirrorCS"),sQuery(id+"F0.wireOp",EDGE,"E140.MirrorCS"),sQuery(id+"F0.wireOp",EDGE,"E141.MirrorCS"),sQuery(id+"F0.wireOp",EDGE,"E142.MirrorCS")])],"isStart":true});
            extrude(context, id + "F3", {"entities" : qUnion([Q0, Q1, Q2, Q3, Q4, Q5, Q6]), "endBound" : BoundingType.UP_TO_SURFACE, "oppositeDirection" : true, "endBoundEntityFace" : qUnion([Q7]), "depth" : 25 * mm});
        }
        {
            var Q0;
            Q0=makeQuery(id+"F3.opExtrude","CAP_FACE",FACE,{"disambiguationData":[OSD([sQuery(id+"F2.wireOp",EDGE,"E143.0.58"),sQuery(id+"F2.wireOp",EDGE,"E143.0.59"),sQuery(id+"F2.wireOp",EDGE,"E143.0.60"),sQuery(id+"F2.wireOp",EDGE,"E144")])],"isStart":true});
            var sketch = newSketch(context, id + "F4", { "sketchPlane" : qUnion([Q0])});
            skPoint(sketch, "E151.0", {"position": v(-150, 100) * mm});
            skPoint(sketch, "E152.0", {"position": v(-146, -80) * mm});
            skLineSegment(sketch, "E153.0", {"start": v(-150, -100) * mm, "end": v(-130, -100) * mm});
            skLineSegment(sketch, "E154.bottom", {"start": v(-150, 100) * mm, "end": v(-146, 100) * mm});
            skLineSegment(sketch, "E154.top", {"start": v(-150, -100) * mm, "end": v(-146, -100) * mm});
            skLineSegment(sketch, "E154.left", {"start": v(-150, 100) * mm, "end": v(-150, -100) * mm});
            skLineSegment(sketch, "E154.right", {"start": v(-146, 100) * mm, "end": v(-146, -100) * mm});
            skSolve(sketch);
        }
        {
            var Q0;
            {var subQ0=sQuery(id+"F4.wireOp",EDGE,"E154.top");Q0=makeQuery(id+"F4.imprint","IMPRINT",FACE,{"disambiguationData":[TD([[makeQuery(id+"F4.imprint","IMPRINT",EDGE,{"derivedFrom":subQ0}),1.0]])]});}
            var Q1;
            {var subQ1=makeQuery(id+"F3.opExtrude","CAP_EDGE",EDGE,{"disambiguationData":[OSD([sQuery(id+"F2.wireOp",EDGE,"E143.0.58")])],"isStart":true});Q1=makeQuery(id+"F4.imprint","IMPRINT",FACE,{"disambiguationData":[TD([[makeQuery(id+"F4.imprint","IMPRINT",EDGE,{"derivedFrom":subQ1}),1.0]])]});}
            var Q2;
            {var subQ0=sQuery(id+"F4.wireOp",EDGE,"E154.bottom");Q2=makeQuery(id+"F4.imprint","IMPRINT",FACE,{"disambiguationData":[TD([[makeQuery(id+"F4.imprint","IMPRINT",EDGE,{"derivedFrom":subQ0}),-1.0]])]});}
            extrude(context, id + "F5", {"entities" : qUnion([Q0, Q1, Q2]), "depth" : 100 * mm});
        }
        {
            var Q0;
            Q0=makeQuery(id+"F3.opExtrude","SWEPT_BODY",BODY,{"disambiguationData":[OSD([sQuery(id+"F2.wireOp",EDGE,"E143.0.58"),sQuery(id+"F2.wireOp",EDGE,"E143.0.59"),sQuery(id+"F2.wireOp",EDGE,"E143.0.60"),sQuery(id+"F2.wireOp",EDGE,"E144")])]});
            var Q1;
            Q1=makeQuery(id+"F3.opExtrude","SWEPT_BODY",BODY,{"disambiguationData":[OSD([sQuery(id+"F2.wireOp",EDGE,"E143.0.62"),sQuery(id+"F2.wireOp",EDGE,"E143.0.63"),sQuery(id+"F2.wireOp",EDGE,"E143.0.64"),sQuery(id+"F2.wireOp",EDGE,"E145")])]});
            var Q2;
            Q2=makeQuery(id+"F3.opExtrude","SWEPT_BODY",BODY,{"disambiguationData":[OSD([sQuery(id+"F2.wireOp",EDGE,"E143.0.66"),sQuery(id+"F2.wireOp",EDGE,"E143.0.67"),sQuery(id+"F2.wireOp",EDGE,"E143.0.68"),sQuery(id+"F2.wireOp",EDGE,"E146")])]});
            var Q3;
            Q3=makeQuery(id+"F3.opExtrude","SWEPT_BODY",BODY,{"disambiguationData":[OSD([sQuery(id+"F2.wireOp",EDGE,"E143.0.70"),sQuery(id+"F2.wireOp",EDGE,"E143.0.71"),sQuery(id+"F2.wireOp",EDGE,"E143.0.72"),sQuery(id+"F2.wireOp",EDGE,"E147")])]});
            var Q4;
            Q4=makeQuery(id+"F3.opExtrude","SWEPT_BODY",BODY,{"disambiguationData":[OSD([sQuery(id+"F2.wireOp",EDGE,"E143.0.74"),sQuery(id+"F2.wireOp",EDGE,"E143.0.75"),sQuery(id+"F2.wireOp",EDGE,"E143.0.76"),sQuery(id+"F2.wireOp",EDGE,"E148")])]});
            var Q5;
            Q5=makeQuery(id+"F3.opExtrude","SWEPT_BODY",BODY,{"disambiguationData":[OSD([sQuery(id+"F2.wireOp",EDGE,"E143.0.78"),sQuery(id+"F2.wireOp",EDGE,"E143.0.79"),sQuery(id+"F2.wireOp",EDGE,"E143.0.80"),sQuery(id+"F2.wireOp",EDGE,"E149")])]});
            var Q6;
            Q6=makeQuery(id+"F3.opExtrude","SWEPT_BODY",BODY,{"disambiguationData":[OSD([sQuery(id+"F2.wireOp",EDGE,"E143.0.82"),sQuery(id+"F2.wireOp",EDGE,"E143.0.83"),sQuery(id+"F2.wireOp",EDGE,"E143.0.84"),sQuery(id+"F2.wireOp",EDGE,"E150")])]});
            var Q7;
            Q7=makeQuery(id+"F5.opExtrude","SWEPT_BODY",BODY,{"disambiguationData":[OSD([sQuery(id+"F4.wireOp",EDGE,"E154.bottom"),sQuery(id+"F4.wireOp",EDGE,"E154.top"),sQuery(id+"F4.wireOp",EDGE,"E154.left"),sQuery(id+"F4.wireOp",EDGE,"E154.right")])]});
            booleanBodies(context, id + "F6", {"operationType" : BooleanOperationType.UNION, "tools" : qUnion([Q0, Q1, Q2, Q3, Q4, Q5, Q6, Q7])});
        }
        {
            var Q0;
            Q0=makeQuery(id+"F6.opBoolean","MERGE",FACE,{"derivedFrom":[makeQuery(id+"F3.opExtrude","SWEPT_FACE",FACE,{"disambiguationData":[OSD([sQuery(id+"F2.wireOp",EDGE,"E143.0.59")])]}),makeQuery(id+"F3.opExtrude","SWEPT_FACE",FACE,{"disambiguationData":[OSD([sQuery(id+"F2.wireOp",EDGE,"E143.0.63")])]}),makeQuery(id+"F3.opExtrude","SWEPT_FACE",FACE,{"disambiguationData":[OSD([sQuery(id+"F2.wireOp",EDGE,"E143.0.67")])]}),makeQuery(id+"F3.opExtrude","SWEPT_FACE",FACE,{"disambiguationData":[OSD([sQuery(id+"F2.wireOp",EDGE,"E143.0.71")])]}),makeQuery(id+"F3.opExtrude","SWEPT_FACE",FACE,{"disambiguationData":[OSD([sQuery(id+"F2.wireOp",EDGE,"E143.0.75")])]}),makeQuery(id+"F3.opExtrude","SWEPT_FACE",FACE,{"disambiguationData":[OSD([sQuery(id+"F2.wireOp",EDGE,"E143.0.79")])]}),makeQuery(id+"F3.opExtrude","SWEPT_FACE",FACE,{"disambiguationData":[OSD([sQuery(id+"F2.wireOp",EDGE,"E143.0.83")])]}),makeQuery(id+"F5.opExtrude","SWEPT_FACE",FACE,{"disambiguationData":[OSD([sQuery(id+"F4.wireOp",EDGE,"E154.right")])]})]});
            var sketch = newSketch(context, id + "F7", { "sketchPlane" : qUnion([Q0])});
            skLineSegment(sketch, "E155", {"start": v(-100, 54) * mm, "end": v(-96, 54) * mm, "construction": true});
            skLineSegment(sketch, "E156", {"start": v(-96, 54) * mm, "end": v(-96, 59) * mm, "construction": true});
            skLineSegment(sketch, "E157", {"start": v(-96, 59) * mm, "end": v(-100, 59) * mm});
            skLineSegment(sketch, "E158.MirrorCS", {"start": v(-96, 49) * mm, "end": v(-100, 49) * mm});
            skLineSegment(sketch, "E159", {"start": v(-96, 49) * mm, "end": v(-96, 59) * mm});
            skLineSegment(sketch, "E160.0.1.0", {"start": v(-96, 79) * mm, "end": v(-100, 79) * mm});
            skLineSegment(sketch, "E160.0.1.1", {"start": v(-96, 69) * mm, "end": v(-96, 79) * mm});
            skLineSegment(sketch, "E160.0.1.2", {"start": v(-96, 69) * mm, "end": v(-100, 69) * mm});
            skLineSegment(sketch, "E160.0.2.0", {"start": v(-96, 99) * mm, "end": v(-100, 99) * mm});
            skLineSegment(sketch, "E160.0.2.1", {"start": v(-96, 89) * mm, "end": v(-96, 99) * mm});
            skLineSegment(sketch, "E160.0.2.2", {"start": v(-96, 89) * mm, "end": v(-100, 89) * mm});
            skLineSegment(sketch, "E160.direction1", {"start": v(-100, 59) * mm, "end": v(-75, 59) * mm, "construction": true});
            skLineSegment(sketch, "E160.direction2", {"start": v(-100, 59) * mm, "end": v(-100, 79) * mm, "construction": true});
            skLineSegment(sketch, "E161.MirrorCS", {"start": v(-96, 19) * mm, "end": v(-96, 9) * mm});
            skLineSegment(sketch, "E162.MirrorCS", {"start": v(-96, 54) * mm, "end": v(-96, 49) * mm, "construction": true});
            skLineSegment(sketch, "E163.MirrorCS", {"start": v(-96, 39) * mm, "end": v(-96, 29) * mm});
            skLineSegment(sketch, "E164.MirrorCS", {"start": v(-96, 9) * mm, "end": v(-100, 9) * mm});
            skLineSegment(sketch, "E165.MirrorCS", {"start": v(-96, 19) * mm, "end": v(-100, 19) * mm});
            skLineSegment(sketch, "E166.MirrorCS", {"start": v(-96, 29) * mm, "end": v(-100, 29) * mm});
            skLineSegment(sketch, "E167.MirrorCS", {"start": v(-100, 49) * mm, "end": v(-100, 29) * mm, "construction": true});
            skLineSegment(sketch, "E168.MirrorCS", {"start": v(-96, 39) * mm, "end": v(-100, 39) * mm});
            skLineSegment(sketch, "E169", {"start": v(-100, 99) * mm, "end": v(-100, 89) * mm});
            skLineSegment(sketch, "E170", {"start": v(-100, 79) * mm, "end": v(-100, 69) * mm});
            skLineSegment(sketch, "E171", {"start": v(-100, 59) * mm, "end": v(-100, 49) * mm});
            skLineSegment(sketch, "E172", {"start": v(-100, 39) * mm, "end": v(-100, 29) * mm});
            skLineSegment(sketch, "E173", {"start": v(-100, 19) * mm, "end": v(-100, 9) * mm});
            skLineSegment(sketch, "E174.MirrorCS", {"start": v(96, 49) * mm, "end": v(100, 49) * mm});
            skLineSegment(sketch, "E175.MirrorCS", {"start": v(96, 49) * mm, "end": v(96, 59) * mm});
            skLineSegment(sketch, "E176.MirrorCS", {"start": v(96, 59) * mm, "end": v(100, 59) * mm});
            skLineSegment(sketch, "E177.MirrorCS", {"start": v(96, 54) * mm, "end": v(96, 59) * mm, "construction": true});
            skLineSegment(sketch, "E178.MirrorCS", {"start": v(96, 54) * mm, "end": v(96, 49) * mm, "construction": true});
            skLineSegment(sketch, "E179.MirrorCS", {"start": v(96, 29) * mm, "end": v(100, 29) * mm});
            skLineSegment(sketch, "E180.MirrorCS", {"start": v(96, 79) * mm, "end": v(100, 79) * mm});
            skLineSegment(sketch, "E181.MirrorCS", {"start": v(96, 19) * mm, "end": v(100, 19) * mm});
            skLineSegment(sketch, "E182.MirrorCS", {"start": v(96, 39) * mm, "end": v(100, 39) * mm});
            skLineSegment(sketch, "E183.MirrorCS", {"start": v(96, 69) * mm, "end": v(100, 69) * mm});
            skLineSegment(sketch, "E184.MirrorCS", {"start": v(96, 9) * mm, "end": v(100, 9) * mm});
            skLineSegment(sketch, "E185.MirrorCS", {"start": v(96, 99) * mm, "end": v(100, 99) * mm});
            skLineSegment(sketch, "E186.MirrorCS", {"start": v(96, 89) * mm, "end": v(100, 89) * mm});
            skLineSegment(sketch, "E187.MirrorCS", {"start": v(100, 54) * mm, "end": v(96, 54) * mm, "construction": true});
            skLineSegment(sketch, "E188.MirrorCS", {"start": v(100, 59) * mm, "end": v(100, 49) * mm});
            skLineSegment(sketch, "E189.MirrorCS", {"start": v(100, 79) * mm, "end": v(100, 69) * mm});
            skLineSegment(sketch, "E190.MirrorCS", {"start": v(100, 39) * mm, "end": v(100, 29) * mm});
            skLineSegment(sketch, "E191.MirrorCS", {"start": v(96, 69) * mm, "end": v(96, 79) * mm});
            skLineSegment(sketch, "E192.MirrorCS", {"start": v(96, 39) * mm, "end": v(96, 29) * mm});
            skLineSegment(sketch, "E193.MirrorCS", {"start": v(100, 19) * mm, "end": v(100, 9) * mm});
            skLineSegment(sketch, "E194.MirrorCS", {"start": v(96, 19) * mm, "end": v(96, 9) * mm});
            skLineSegment(sketch, "E195.MirrorCS", {"start": v(96, 89) * mm, "end": v(96, 99) * mm});
            skLineSegment(sketch, "E196.MirrorCS", {"start": v(100, 99) * mm, "end": v(100, 89) * mm});
            skLineSegment(sketch, "E197.MirrorCS", {"start": v(100, 59) * mm, "end": v(100, 79) * mm, "construction": true});
            skLineSegment(sketch, "E198.MirrorCS", {"start": v(100, 49) * mm, "end": v(100, 29) * mm, "construction": true});
            skSolve(sketch);
        }
        {
            var Q0;
            Q0 = qSketchRegion(id + "F7", true);
            var Q1;
            Q1=makeQuery(id+"F6.opBoolean","MERGE",FACE,{"derivedFrom":[makeQuery(id+"F3.opExtrude","SWEPT_FACE",FACE,{"disambiguationData":[OSD([sQuery(id+"F2.wireOp",EDGE,"E144")])]}),makeQuery(id+"F3.opExtrude","SWEPT_FACE",FACE,{"disambiguationData":[OSD([sQuery(id+"F2.wireOp",EDGE,"E145")])]}),makeQuery(id+"F3.opExtrude","SWEPT_FACE",FACE,{"disambiguationData":[OSD([sQuery(id+"F2.wireOp",EDGE,"E146")])]}),makeQuery(id+"F3.opExtrude","SWEPT_FACE",FACE,{"disambiguationData":[OSD([sQuery(id+"F2.wireOp",EDGE,"E147")])]}),makeQuery(id+"F3.opExtrude","SWEPT_FACE",FACE,{"disambiguationData":[OSD([sQuery(id+"F2.wireOp",EDGE,"E148")])]}),makeQuery(id+"F3.opExtrude","SWEPT_FACE",FACE,{"disambiguationData":[OSD([sQuery(id+"F2.wireOp",EDGE,"E149")])]}),makeQuery(id+"F3.opExtrude","SWEPT_FACE",FACE,{"disambiguationData":[OSD([sQuery(id+"F2.wireOp",EDGE,"E150")])]}),makeQuery(id+"F5.opExtrude","SWEPT_FACE",FACE,{"disambiguationData":[OSD([sQuery(id+"F4.wireOp",EDGE,"E154.left")])]})]});
            extrude(context, id + "F8", {"entities" : qUnion([Q0]), "operationType" : NewBodyOperationType.REMOVE, "endBound" : BoundingType.UP_TO_SURFACE, "oppositeDirection" : true, "endBoundEntityFace" : qUnion([Q1]), "depth" : 25 * mm});
        }
        {
            var Q0;
            Q0=makeQuery(id+"F3.opExtrude","SWEPT_BODY",BODY,{"disambiguationData":[OSD([sQuery(id+"F2.wireOp",EDGE,"E143.0.58"),sQuery(id+"F2.wireOp",EDGE,"E143.0.59"),sQuery(id+"F2.wireOp",EDGE,"E143.0.60"),sQuery(id+"F2.wireOp",EDGE,"E144")])]});
            var Q1;
            Q1=qCreatedBy(makeId("Right.planeOp"),FACE);
            mirror(context, id + "F9", {"entities" : qUnion([Q0]), "mirrorPlane" : qUnion([Q1])});
        }
        {
            var Q0;
            Q0=makeQuery(id+"F1.opExtrude","CAP_FACE",FACE,{"disambiguationData":[OSD([sQuery(id+"F0.wireOp",EDGE,"E2"),sQuery(id+"F0.wireOp",EDGE,"E4"),sQuery(id+"F0.wireOp",EDGE,"E6.0.1.0"),sQuery(id+"F0.wireOp",EDGE,"E6.0.1.1"),sQuery(id+"F0.wireOp",EDGE,"E6.0.1.2"),sQuery(id+"F0.wireOp",EDGE,"E6.0.2.0"),sQuery(id+"F0.wireOp",EDGE,"E6.0.2.1"),sQuery(id+"F0.wireOp",EDGE,"E6.0.2.2"),sQuery(id+"F0.wireOp",EDGE,"E6.0.3.0"),sQuery(id+"F0.wireOp",EDGE,"E6.0.3.1"),sQuery(id+"F0.wireOp",EDGE,"E6.0.3.2"),sQuery(id+"F0.wireOp",EDGE,"E7.MirrorCS"),sQuery(id+"F0.wireOp",EDGE,"E3.MirrorCS"),sQuery(id+"F0.wireOp",EDGE,"E8.MirrorCS"),sQuery(id+"F0.wireOp",EDGE,"E9.MirrorCS"),sQuery(id+"F0.wireOp",EDGE,"E10.MirrorCS"),sQuery(id+"F0.wireOp",EDGE,"E11.MirrorCS"),sQuery(id+"F0.wireOp",EDGE,"E12.MirrorCS"),sQuery(id+"F0.wireOp",EDGE,"E13.MirrorCS"),sQuery(id+"F0.wireOp",EDGE,"E14.MirrorCS"),sQuery(id+"F0.wireOp",EDGE,"E15.MirrorCS"),sQuery(id+"F0.wireOp",EDGE,"E17"),sQuery(id+"F0.wireOp",EDGE,"E18"),sQuery(id+"F0.wireOp",EDGE,"E19"),sQuery(id+"F0.wireOp",EDGE,"E20"),sQuery(id+"F0.wireOp",EDGE,"E21"),sQuery(id+"F0.wireOp",EDGE,"E22"),sQuery(id+"F0.wireOp",EDGE,"E23"),sQuery(id+"F0.wireOp",EDGE,"E24"),sQuery(id+"F0.wireOp",EDGE,"E27.MirrorCS"),sQuery(id+"F0.wireOp",EDGE,"E26.MirrorCS"),sQuery(id+"F0.wireOp",EDGE,"E28.MirrorCS"),sQuery(id+"F0.wireOp",EDGE,"E29.MirrorCS"),sQuery(id+"F0.wireOp",EDGE,"E30.MirrorCS"),sQuery(id+"F0.wireOp",EDGE,"E31.MirrorCS"),sQuery(id+"F0.wireOp",EDGE,"E32.MirrorCS"),sQuery(id+"F0.wireOp",EDGE,"E33.MirrorCS"),sQuery(id+"F0.wireOp",EDGE,"E34.MirrorCS"),sQuery(id+"F0.wireOp",EDGE,"E35.MirrorCS"),sQuery(id+"F0.wireOp",EDGE,"E36.MirrorCS"),sQuery(id+"F0.wireOp",EDGE,"E37.MirrorCS"),sQuery(id+"F0.wireOp",EDGE,"E38.MirrorCS"),sQuery(id+"F0.wireOp",EDGE,"E39.MirrorCS"),sQuery(id+"F0.wireOp",EDGE,"E40.MirrorCS"),sQuery(id+"F0.wireOp",EDGE,"E41.MirrorCS"),sQuery(id+"F0.wireOp",EDGE,"E43.MirrorCS"),sQuery(id+"F0.wireOp",EDGE,"E44.MirrorCS"),sQuery(id+"F0.wireOp",EDGE,"E45.MirrorCS"),sQuery(id+"F0.wireOp",EDGE,"E46.MirrorCS"),sQuery(id+"F0.wireOp",EDGE,"E47.MirrorCS"),sQuery(id+"F0.wireOp",EDGE,"E48.MirrorCS"),sQuery(id+"F0.wireOp",EDGE,"E49.MirrorCS"),sQuery(id+"F0.wireOp",EDGE,"E50.MirrorCS"),sQuery(id+"F0.wireOp",EDGE,"E51.MirrorCS"),sQuery(id+"F0.wireOp",EDGE,"E52.MirrorCS"),sQuery(id+"F0.wireOp",EDGE,"E53.MirrorCS"),sQuery(id+"F0.wireOp",EDGE,"E54"),sQuery(id+"F0.wireOp",EDGE,"E55"),sQuery(id+"F0.wireOp",EDGE,"E61.1.0.0"),sQuery(id+"F0.wireOp",EDGE,"E61.1.0.1"),sQuery(id+"F0.wireOp",EDGE,"E61.1.0.2"),sQuery(id+"F0.wireOp",EDGE,"E61.2.0.0"),sQuery(id+"F0.wireOp",EDGE,"E61.2.0.1"),sQuery(id+"F0.wireOp",EDGE,"E61.2.0.2"),sQuery(id+"F0.wireOp",EDGE,"E61.3.0.0"),sQuery(id+"F0.wireOp",EDGE,"E61.3.0.1"),sQuery(id+"F0.wireOp",EDGE,"E61.3.0.2"),sQuery(id+"F0.wireOp",EDGE,"E61.4.0.0"),sQuery(id+"F0.wireOp",EDGE,"E61.4.0.1"),sQuery(id+"F0.wireOp",EDGE,"E61.4.0.2"),sQuery(id+"F0.wireOp",EDGE,"E61.5.0.0"),sQuery(id+"F0.wireOp",EDGE,"E61.5.0.1"),sQuery(id+"F0.wireOp",EDGE,"E61.5.0.2"),sQuery(id+"F0.wireOp",EDGE,"E62.MirrorCS"),sQuery(id+"F0.wireOp",EDGE,"E64.MirrorCS"),sQuery(id+"F0.wireOp",EDGE,"E65.MirrorCS"),sQuery(id+"F0.wireOp",EDGE,"E66.MirrorCS"),sQuery(id+"F0.wireOp",EDGE,"E67.MirrorCS"),sQuery(id+"F0.wireOp",EDGE,"E68.MirrorCS"),sQuery(id+"F0.wireOp",EDGE,"E69.MirrorCS"),sQuery(id+"F0.wireOp",EDGE,"E70.MirrorCS"),sQuery(id+"F0.wireOp",EDGE,"E59.MirrorCS"),sQuery(id+"F0.wireOp",EDGE,"E58"),sQuery(id+"F0.wireOp",EDGE,"E71.MirrorCS"),sQuery(id+"F0.wireOp",EDGE,"E72.MirrorCS"),sQuery(id+"F0.wireOp",EDGE,"E73.MirrorCS"),sQuery(id+"F0.wireOp",EDGE,"E74.MirrorCS"),sQuery(id+"F0.wireOp",EDGE,"E76.MirrorCS"),sQuery(id+"F0.wireOp",EDGE,"E77.MirrorCS"),sQuery(id+"F0.wireOp",EDGE,"E78.MirrorCS"),sQuery(id+"F0.wireOp",EDGE,"E79.MirrorCS"),sQuery(id+"F0.wireOp",EDGE,"E80"),sQuery(id+"F0.wireOp",EDGE,"E81"),sQuery(id+"F0.wireOp",EDGE,"E82"),sQuery(id+"F0.wireOp",EDGE,"E83"),sQuery(id+"F0.wireOp",EDGE,"E84"),sQuery(id+"F0.wireOp",EDGE,"E85"),sQuery(id+"F0.wireOp",EDGE,"E86"),sQuery(id+"F0.wireOp",EDGE,"E87"),sQuery(id+"F0.wireOp",EDGE,"E88"),sQuery(id+"F0.wireOp",EDGE,"E89"),sQuery(id+"F0.wireOp",EDGE,"E90"),sQuery(id+"F0.wireOp",EDGE,"E91"),sQuery(id+"F0.wireOp",EDGE,"E93.MirrorCS"),sQuery(id+"F0.wireOp",EDGE,"E95.MirrorCS"),sQuery(id+"F0.wireOp",EDGE,"E94.MirrorCS"),sQuery(id+"F0.wireOp",EDGE,"E98.MirrorCS"),sQuery(id+"F0.wireOp",EDGE,"E99.MirrorCS"),sQuery(id+"F0.wireOp",EDGE,"E100.MirrorCS"),sQuery(id+"F0.wireOp",EDGE,"E101.MirrorCS"),sQuery(id+"F0.wireOp",EDGE,"E102.MirrorCS"),sQuery(id+"F0.wireOp",EDGE,"E103.MirrorCS"),sQuery(id+"F0.wireOp",EDGE,"E104.MirrorCS"),sQuery(id+"F0.wireOp",EDGE,"E105.MirrorCS"),sQuery(id+"F0.wireOp",EDGE,"E106.MirrorCS"),sQuery(id+"F0.wireOp",EDGE,"E107.MirrorCS"),sQuery(id+"F0.wireOp",EDGE,"E108.MirrorCS"),sQuery(id+"F0.wireOp",EDGE,"E109.MirrorCS"),sQuery(id+"F0.wireOp",EDGE,"E110.MirrorCS"),sQuery(id+"F0.wireOp",EDGE,"E111.MirrorCS"),sQuery(id+"F0.wireOp",EDGE,"E112.MirrorCS"),sQuery(id+"F0.wireOp",EDGE,"E113.MirrorCS"),sQuery(id+"F0.wireOp",EDGE,"E114.MirrorCS"),sQuery(id+"F0.wireOp",EDGE,"E115.MirrorCS"),sQuery(id+"F0.wireOp",EDGE,"E116.MirrorCS"),sQuery(id+"F0.wireOp",EDGE,"E117.MirrorCS"),sQuery(id+"F0.wireOp",EDGE,"E119.MirrorCS"),sQuery(id+"F0.wireOp",EDGE,"E120.MirrorCS"),sQuery(id+"F0.wireOp",EDGE,"E121.MirrorCS"),sQuery(id+"F0.wireOp",EDGE,"E122.MirrorCS"),sQuery(id+"F0.wireOp",EDGE,"E123.MirrorCS"),sQuery(id+"F0.wireOp",EDGE,"E124.MirrorCS"),sQuery(id+"F0.wireOp",EDGE,"E125.MirrorCS"),sQuery(id+"F0.wireOp",EDGE,"E126.MirrorCS"),sQuery(id+"F0.wireOp",EDGE,"E127.MirrorCS"),sQuery(id+"F0.wireOp",EDGE,"E128.MirrorCS"),sQuery(id+"F0.wireOp",EDGE,"E129.MirrorCS"),sQuery(id+"F0.wireOp",EDGE,"E130.MirrorCS"),sQuery(id+"F0.wireOp",EDGE,"E131.MirrorCS"),sQuery(id+"F0.wireOp",EDGE,"E132.MirrorCS"),sQuery(id+"F0.wireOp",EDGE,"E135.MirrorCS"),sQuery(id+"F0.wireOp",EDGE,"E136.MirrorCS"),sQuery(id+"F0.wireOp",EDGE,"E137.MirrorCS"),sQuery(id+"F0.wireOp",EDGE,"E138.MirrorCS"),sQuery(id+"F0.wireOp",EDGE,"E139.MirrorCS"),sQuery(id+"F0.wireOp",EDGE,"E140.MirrorCS"),sQuery(id+"F0.wireOp",EDGE,"E141.MirrorCS"),sQuery(id+"F0.wireOp",EDGE,"E142.MirrorCS")])],"isStart":false});
            var sketch = newSketch(context, id + "F10", { "sketchPlane" : qUnion([Q0])});
            skLineSegment(sketch, "E199.0", {"start": v(-70, 100) * mm, "end": v(-55, 100) * mm});
            skLineSegment(sketch, "E199.1", {"start": v(105, 100) * mm, "end": v(120, 100) * mm});
            skLineSegment(sketch, "E199.2", {"start": v(-105, 96) * mm, "end": v(-105, 100) * mm});
            skLineSegment(sketch, "E199.3", {"start": v(-30, -96) * mm, "end": v(-30, -100) * mm});
            skLineSegment(sketch, "E199.4", {"start": v(-20, -96) * mm, "end": v(-30, -96) * mm});
            skLineSegment(sketch, "E199.5", {"start": v(45, 96) * mm, "end": v(45, 100) * mm});
            skLineSegment(sketch, "E199.6", {"start": v(-120, -96) * mm, "end": v(-120, -100) * mm});
            skLineSegment(sketch, "E199.7", {"start": v(105, 96) * mm, "end": v(105, 100) * mm});
            skLineSegment(sketch, "E199.8", {"start": v(-95, 100) * mm, "end": v(-80, 100) * mm});
            skLineSegment(sketch, "E199.10", {"start": v(-45, 96) * mm, "end": v(-45, 100) * mm});
            skLineSegment(sketch, "E199.11", {"start": v(-70, 96) * mm, "end": v(-70, 100) * mm});
            skLineSegment(sketch, "E199.12", {"start": v(-120, 100) * mm, "end": v(-105, 100) * mm});
            skLineSegment(sketch, "E199.13", {"start": v(80, 100) * mm, "end": v(95, 100) * mm});
            skLineSegment(sketch, "E199.14", {"start": v(70, -96) * mm, "end": v(80, -96) * mm});
            skLineSegment(sketch, "E199.15", {"start": v(5, -100) * mm, "end": v(20, -100) * mm});
            skLineSegment(sketch, "E199.16", {"start": v(20, 96) * mm, "end": v(30, 96) * mm});
            skLineSegment(sketch, "E199.17", {"start": v(-120, 96) * mm, "end": v(-120, 100) * mm});
            skLineSegment(sketch, "E199.18", {"start": v(-95, -100) * mm, "end": v(-80, -100) * mm});
            skLineSegment(sketch, "E199.19", {"start": v(-20, -96) * mm, "end": v(-20, -100) * mm});
            skLineSegment(sketch, "E199.20", {"start": v(-20, -100) * mm, "end": v(-5, -100) * mm});
            skLineSegment(sketch, "E199.21", {"start": v(-45, -96) * mm, "end": v(-45, -100) * mm});
            skLineSegment(sketch, "E199.22", {"start": v(80, -96) * mm, "end": v(80, -100) * mm});
            skLineSegment(sketch, "E199.23", {"start": v(-80, 96) * mm, "end": v(-80, 100) * mm});
            skLineSegment(sketch, "E199.24", {"start": v(-105, -96) * mm, "end": v(-105, -100) * mm});
            skLineSegment(sketch, "E199.25", {"start": v(95, 96) * mm, "end": v(105, 96) * mm});
            skLineSegment(sketch, "E199.26", {"start": v(-130, 96) * mm, "end": v(-130, 100) * mm});
            skLineSegment(sketch, "E199.27", {"start": v(55, 96) * mm, "end": v(55, 100) * mm});
            skLineSegment(sketch, "E199.28", {"start": v(120, 96) * mm, "end": v(120, 100) * mm});
            skLineSegment(sketch, "E199.32", {"start": v(120, -96) * mm, "end": v(120, -100) * mm});
            skLineSegment(sketch, "E199.33", {"start": v(-130, -96) * mm, "end": v(-130, -100) * mm});
            skLineSegment(sketch, "E199.34", {"start": v(-45, -96) * mm, "end": v(-55, -96) * mm});
            skLineSegment(sketch, "E199.35", {"start": v(-70, 96) * mm, "end": v(-80, 96) * mm});
            skLineSegment(sketch, "E199.36", {"start": v(-95, 96) * mm, "end": v(-105, 96) * mm});
            skLineSegment(sketch, "E199.37", {"start": v(-20, 100) * mm, "end": v(-5, 100) * mm});
            skLineSegment(sketch, "E199.38", {"start": v(45, 96) * mm, "end": v(55, 96) * mm});
            skLineSegment(sketch, "E199.39", {"start": v(130, 96) * mm, "end": v(130, 100) * mm});
            skLineSegment(sketch, "E199.40", {"start": v(-45, 96) * mm, "end": v(-55, 96) * mm});
            skLineSegment(sketch, "E199.41", {"start": v(-30, 96) * mm, "end": v(-30, 100) * mm});
            skLineSegment(sketch, "E199.42", {"start": v(-45, 100) * mm, "end": v(-30, 100) * mm});
            skLineSegment(sketch, "E199.43", {"start": v(5, -96) * mm, "end": v(-5, -96) * mm});
            skLineSegment(sketch, "E199.44", {"start": v(105, -96) * mm, "end": v(105, -100) * mm});
            skLineSegment(sketch, "E199.45", {"start": v(95, -96) * mm, "end": v(95, -100) * mm});
            skLineSegment(sketch, "E199.46", {"start": v(30, -100) * mm, "end": v(45, -100) * mm});
            skLineSegment(sketch, "E199.47", {"start": v(20, -96) * mm, "end": v(30, -96) * mm});
            skLineSegment(sketch, "E199.48", {"start": v(120, -96) * mm, "end": v(130, -96) * mm});
            skLineSegment(sketch, "E199.49", {"start": v(5, -96) * mm, "end": v(5, -100) * mm});
            skLineSegment(sketch, "E199.50", {"start": v(30, -96) * mm, "end": v(30, -100) * mm});
            skLineSegment(sketch, "E199.51", {"start": v(-70, -96) * mm, "end": v(-70, -100) * mm});
            skLineSegment(sketch, "E199.52", {"start": v(-120, -96) * mm, "end": v(-130, -96) * mm});
            skLineSegment(sketch, "E199.53", {"start": v(105, -100) * mm, "end": v(120, -100) * mm});
            skLineSegment(sketch, "E199.54", {"start": v(-70, -96) * mm, "end": v(-80, -96) * mm});
            skLineSegment(sketch, "E199.56", {"start": v(70, 96) * mm, "end": v(70, 100) * mm});
            skLineSegment(sketch, "E199.57", {"start": v(120, 96) * mm, "end": v(130, 96) * mm});
            skLineSegment(sketch, "E199.58", {"start": v(80, 96) * mm, "end": v(80, 100) * mm});
            skLineSegment(sketch, "E199.59", {"start": v(5, 96) * mm, "end": v(-5, 96) * mm});
            skLineSegment(sketch, "E199.60", {"start": v(-5, 96) * mm, "end": v(-5, 100) * mm});
            skLineSegment(sketch, "E199.61", {"start": v(-20, 96) * mm, "end": v(-30, 96) * mm});
            skLineSegment(sketch, "E199.62", {"start": v(5, 100) * mm, "end": v(20, 100) * mm});
            skLineSegment(sketch, "E199.63", {"start": v(-5, -96) * mm, "end": v(-5, -100) * mm});
            skLineSegment(sketch, "E199.64", {"start": v(20, -96) * mm, "end": v(20, -100) * mm});
            skLineSegment(sketch, "E199.65", {"start": v(-95, -96) * mm, "end": v(-95, -100) * mm});
            skLineSegment(sketch, "E199.66", {"start": v(45, -96) * mm, "end": v(55, -96) * mm});
            skLineSegment(sketch, "E199.67", {"start": v(80, -100) * mm, "end": v(95, -100) * mm});
            skLineSegment(sketch, "E199.68", {"start": v(20, 96) * mm, "end": v(20, 100) * mm});
            skLineSegment(sketch, "E199.69", {"start": v(70, 96) * mm, "end": v(80, 96) * mm});
            skLineSegment(sketch, "E199.70", {"start": v(-95, 96) * mm, "end": v(-95, 100) * mm});
            skLineSegment(sketch, "E199.71", {"start": v(5, 96) * mm, "end": v(5, 100) * mm});
            skLineSegment(sketch, "E199.72", {"start": v(-120, 96) * mm, "end": v(-130, 96) * mm});
            skLineSegment(sketch, "E199.73", {"start": v(30, 100) * mm, "end": v(45, 100) * mm});
            skLineSegment(sketch, "E199.74", {"start": v(-55, -96) * mm, "end": v(-55, -100) * mm});
            skLineSegment(sketch, "E199.75", {"start": v(130, -96) * mm, "end": v(130, -100) * mm});
            skLineSegment(sketch, "E199.76", {"start": v(55, -96) * mm, "end": v(55, -100) * mm});
            skLineSegment(sketch, "E199.77", {"start": v(-120, -100) * mm, "end": v(-105, -100) * mm});
            skLineSegment(sketch, "E199.78", {"start": v(55, -100) * mm, "end": v(70, -100) * mm});
            skLineSegment(sketch, "E199.79", {"start": v(-70, -100) * mm, "end": v(-55, -100) * mm});
            skLineSegment(sketch, "E199.80", {"start": v(30, 96) * mm, "end": v(30, 100) * mm});
            skLineSegment(sketch, "E199.81", {"start": v(95, 96) * mm, "end": v(95, 100) * mm});
            skLineSegment(sketch, "E199.82", {"start": v(-20, 96) * mm, "end": v(-20, 100) * mm});
            skLineSegment(sketch, "E199.83", {"start": v(-55, 96) * mm, "end": v(-55, 100) * mm});
            skLineSegment(sketch, "E199.84", {"start": v(55, 100) * mm, "end": v(70, 100) * mm});
            skLineSegment(sketch, "E199.85", {"start": v(45, -96) * mm, "end": v(45, -100) * mm});
            skLineSegment(sketch, "E199.86", {"start": v(-80, -96) * mm, "end": v(-80, -100) * mm});
            skLineSegment(sketch, "E199.87", {"start": v(70, -96) * mm, "end": v(70, -100) * mm});
            skLineSegment(sketch, "E199.88", {"start": v(-95, -96) * mm, "end": v(-105, -96) * mm});
            skLineSegment(sketch, "E199.89", {"start": v(-45, -100) * mm, "end": v(-30, -100) * mm});
            skLineSegment(sketch, "E199.90", {"start": v(95, -96) * mm, "end": v(105, -96) * mm});
            skLineSegment(sketch, "E199.91", {"start": v(70, -96) * mm, "end": v(80, -96) * mm});
            skLineSegment(sketch, "E199.93", {"start": v(-45, 96) * mm, "end": v(-45, 100) * mm});
            skLineSegment(sketch, "E199.94", {"start": v(-20, -96) * mm, "end": v(-30, -96) * mm});
            skLineSegment(sketch, "E199.98", {"start": v(120, -96) * mm, "end": v(120, -100) * mm});
            skLineSegment(sketch, "E199.101", {"start": v(5, -100) * mm, "end": v(20, -100) * mm});
            skLineSegment(sketch, "E199.104", {"start": v(120, 96) * mm, "end": v(120, 100) * mm});
            skLineSegment(sketch, "E199.106", {"start": v(-120, -96) * mm, "end": v(-120, -100) * mm});
            skLineSegment(sketch, "E199.107", {"start": v(-70, 96) * mm, "end": v(-80, 96) * mm});
            skLineSegment(sketch, "E199.108", {"start": v(-105, 96) * mm, "end": v(-105, 100) * mm});
            skLineSegment(sketch, "E199.110", {"start": v(45, 96) * mm, "end": v(45, 100) * mm});
            skLineSegment(sketch, "E199.113", {"start": v(-105, -96) * mm, "end": v(-105, -100) * mm});
            skLineSegment(sketch, "E199.116", {"start": v(95, 96) * mm, "end": v(105, 96) * mm});
            skLineSegment(sketch, "E199.120", {"start": v(-70, 100) * mm, "end": v(-55, 100) * mm});
            skLineSegment(sketch, "E199.121", {"start": v(-130, 96) * mm, "end": v(-130, 100) * mm});
            skLineSegment(sketch, "E199.122", {"start": v(-95, 100) * mm, "end": v(-80, 100) * mm});
            skLineSegment(sketch, "E199.123", {"start": v(55, 96) * mm, "end": v(55, 100) * mm});
            skLineSegment(sketch, "E199.124", {"start": v(105, 100) * mm, "end": v(120, 100) * mm});
            skLineSegment(sketch, "E199.125", {"start": v(-130, -96) * mm, "end": v(-130, -100) * mm});
            skLineSegment(sketch, "E199.135", {"start": v(-45, -96) * mm, "end": v(-55, -96) * mm});
            skLineSegment(sketch, "E199.136", {"start": v(-30, -96) * mm, "end": v(-30, -100) * mm});
            skLineSegment(sketch, "E199.143", {"start": v(45, 96) * mm, "end": v(55, 96) * mm});
            skLineSegment(sketch, "E199.144", {"start": v(-30, 96) * mm, "end": v(-30, 100) * mm});
            skLineSegment(sketch, "E199.145", {"start": v(130, 96) * mm, "end": v(130, 100) * mm});
            skLineSegment(sketch, "E199.146", {"start": v(-45, 96) * mm, "end": v(-55, 96) * mm});
            skLineSegment(sketch, "E199.147", {"start": v(-45, 100) * mm, "end": v(-30, 100) * mm});
            skLineSegment(sketch, "E199.148", {"start": v(5, -96) * mm, "end": v(-5, -96) * mm});
            skLineSegment(sketch, "E199.149", {"start": v(105, -96) * mm, "end": v(105, -100) * mm});
            skLineSegment(sketch, "E199.150", {"start": v(95, -96) * mm, "end": v(95, -100) * mm});
            skLineSegment(sketch, "E199.151", {"start": v(30, -100) * mm, "end": v(45, -100) * mm});
            skLineSegment(sketch, "E199.152", {"start": v(20, -96) * mm, "end": v(30, -96) * mm});
            skLineSegment(sketch, "E199.153", {"start": v(120, -96) * mm, "end": v(130, -96) * mm});
            skLineSegment(sketch, "E199.164", {"start": v(70, 96) * mm, "end": v(70, 100) * mm});
            skLineSegment(sketch, "E199.165", {"start": v(120, 96) * mm, "end": v(130, 96) * mm});
            skLineSegment(sketch, "E199.166", {"start": v(-80, 96) * mm, "end": v(-80, 100) * mm});
            skLineSegment(sketch, "E199.167", {"start": v(-95, 96) * mm, "end": v(-105, 96) * mm});
            skLineSegment(sketch, "E199.168", {"start": v(-20, 100) * mm, "end": v(-5, 100) * mm});
            skLineSegment(sketch, "E199.169", {"start": v(5, -96) * mm, "end": v(5, -100) * mm});
            skLineSegment(sketch, "E199.170", {"start": v(30, -96) * mm, "end": v(30, -100) * mm});
            skLineSegment(sketch, "E199.171", {"start": v(-70, -96) * mm, "end": v(-70, -100) * mm});
            skLineSegment(sketch, "E199.172", {"start": v(-120, -96) * mm, "end": v(-130, -96) * mm});
            skLineSegment(sketch, "E199.173", {"start": v(105, -100) * mm, "end": v(120, -100) * mm});
            skLineSegment(sketch, "E199.174", {"start": v(-70, -96) * mm, "end": v(-80, -96) * mm});
            skLineSegment(sketch, "E199.185", {"start": v(80, 96) * mm, "end": v(80, 100) * mm});
            skLineSegment(sketch, "E199.186", {"start": v(5, 96) * mm, "end": v(-5, 96) * mm});
            skLineSegment(sketch, "E199.187", {"start": v(-5, 96) * mm, "end": v(-5, 100) * mm});
            skLineSegment(sketch, "E199.188", {"start": v(-20, 96) * mm, "end": v(-30, 96) * mm});
            skLineSegment(sketch, "E199.189", {"start": v(5, 100) * mm, "end": v(20, 100) * mm});
            skLineSegment(sketch, "E199.190", {"start": v(-5, -96) * mm, "end": v(-5, -100) * mm});
            skLineSegment(sketch, "E199.191", {"start": v(20, -96) * mm, "end": v(20, -100) * mm});
            skLineSegment(sketch, "E199.192", {"start": v(-95, -96) * mm, "end": v(-95, -100) * mm});
            skLineSegment(sketch, "E199.193", {"start": v(45, -96) * mm, "end": v(55, -96) * mm});
            skLineSegment(sketch, "E199.194", {"start": v(80, -100) * mm, "end": v(95, -100) * mm});
            skLineSegment(sketch, "E199.205", {"start": v(20, 96) * mm, "end": v(20, 100) * mm});
            skLineSegment(sketch, "E199.206", {"start": v(70, 96) * mm, "end": v(80, 96) * mm});
            skLineSegment(sketch, "E199.207", {"start": v(-95, 96) * mm, "end": v(-95, 100) * mm});
            skLineSegment(sketch, "E199.208", {"start": v(5, 96) * mm, "end": v(5, 100) * mm});
            skLineSegment(sketch, "E199.209", {"start": v(-120, 96) * mm, "end": v(-130, 96) * mm});
            skLineSegment(sketch, "E199.210", {"start": v(30, 100) * mm, "end": v(45, 100) * mm});
            skLineSegment(sketch, "E199.211", {"start": v(-55, -96) * mm, "end": v(-55, -100) * mm});
            skLineSegment(sketch, "E199.212", {"start": v(130, -96) * mm, "end": v(130, -100) * mm});
            skLineSegment(sketch, "E199.213", {"start": v(55, -96) * mm, "end": v(55, -100) * mm});
            skLineSegment(sketch, "E199.214", {"start": v(-120, -100) * mm, "end": v(-105, -100) * mm});
            skLineSegment(sketch, "E199.215", {"start": v(55, -100) * mm, "end": v(70, -100) * mm});
            skLineSegment(sketch, "E199.216", {"start": v(-70, -100) * mm, "end": v(-55, -100) * mm});
            skLineSegment(sketch, "E199.227", {"start": v(30, 96) * mm, "end": v(30, 100) * mm});
            skLineSegment(sketch, "E199.228", {"start": v(95, 96) * mm, "end": v(95, 100) * mm});
            skLineSegment(sketch, "E199.229", {"start": v(-20, 96) * mm, "end": v(-20, 100) * mm});
            skLineSegment(sketch, "E199.230", {"start": v(-55, 96) * mm, "end": v(-55, 100) * mm});
            skLineSegment(sketch, "E199.231", {"start": v(55, 100) * mm, "end": v(70, 100) * mm});
            skLineSegment(sketch, "E199.232", {"start": v(45, -96) * mm, "end": v(45, -100) * mm});
            skLineSegment(sketch, "E199.233", {"start": v(-80, -96) * mm, "end": v(-80, -100) * mm});
            skLineSegment(sketch, "E199.234", {"start": v(70, -96) * mm, "end": v(70, -100) * mm});
            skLineSegment(sketch, "E199.235", {"start": v(-95, -96) * mm, "end": v(-105, -96) * mm});
            skLineSegment(sketch, "E199.236", {"start": v(-45, -100) * mm, "end": v(-30, -100) * mm});
            skLineSegment(sketch, "E199.237", {"start": v(95, -96) * mm, "end": v(105, -96) * mm});
            skLineSegment(sketch, "E199.249", {"start": v(20, 96) * mm, "end": v(30, 96) * mm});
            skLineSegment(sketch, "E199.250", {"start": v(105, 96) * mm, "end": v(105, 100) * mm});
            skLineSegment(sketch, "E199.251", {"start": v(-120, 96) * mm, "end": v(-120, 100) * mm});
            skLineSegment(sketch, "E199.252", {"start": v(-70, 96) * mm, "end": v(-70, 100) * mm});
            skLineSegment(sketch, "E199.253", {"start": v(-120, 100) * mm, "end": v(-105, 100) * mm});
            skLineSegment(sketch, "E199.254", {"start": v(80, 100) * mm, "end": v(95, 100) * mm});
            skLineSegment(sketch, "E199.255", {"start": v(-20, -96) * mm, "end": v(-20, -100) * mm});
            skLineSegment(sketch, "E199.256", {"start": v(80, -96) * mm, "end": v(80, -100) * mm});
            skLineSegment(sketch, "E199.257", {"start": v(-45, -96) * mm, "end": v(-45, -100) * mm});
            skLineSegment(sketch, "E199.258", {"start": v(-20, -100) * mm, "end": v(-5, -100) * mm});
            skLineSegment(sketch, "E199.259", {"start": v(-95, -100) * mm, "end": v(-80, -100) * mm});
            skLineSegment(sketch, "E200", {"start": v(-130, 100) * mm, "end": v(-120, 100) * mm});
            skLineSegment(sketch, "E201", {"start": v(-105, 100) * mm, "end": v(-95, 100) * mm});
            skLineSegment(sketch, "E202", {"start": v(-80, 100) * mm, "end": v(-70, 100) * mm});
            skLineSegment(sketch, "E203", {"start": v(-55, 100) * mm, "end": v(-45, 100) * mm});
            skLineSegment(sketch, "E204", {"start": v(-30, 100) * mm, "end": v(-20, 100) * mm});
            skLineSegment(sketch, "E205", {"start": v(-5, 100) * mm, "end": v(130, 100) * mm});
            skLineSegment(sketch, "E206", {"start": v(-130, -100) * mm, "end": v(130, -100) * mm});
            skSolve(sketch);
        }
        {
            var Q0;
            Q0 = qSketchRegion(id + "F10", true);
            var Q1;
            Q1=makeQuery(id+"F1.opExtrude","CAP_FACE",FACE,{"disambiguationData":[OSD([sQuery(id+"F0.wireOp",EDGE,"E2"),sQuery(id+"F0.wireOp",EDGE,"E4"),sQuery(id+"F0.wireOp",EDGE,"E6.0.1.0"),sQuery(id+"F0.wireOp",EDGE,"E6.0.1.1"),sQuery(id+"F0.wireOp",EDGE,"E6.0.1.2"),sQuery(id+"F0.wireOp",EDGE,"E6.0.2.0"),sQuery(id+"F0.wireOp",EDGE,"E6.0.2.1"),sQuery(id+"F0.wireOp",EDGE,"E6.0.2.2"),sQuery(id+"F0.wireOp",EDGE,"E6.0.3.0"),sQuery(id+"F0.wireOp",EDGE,"E6.0.3.1"),sQuery(id+"F0.wireOp",EDGE,"E6.0.3.2"),sQuery(id+"F0.wireOp",EDGE,"E7.MirrorCS"),sQuery(id+"F0.wireOp",EDGE,"E3.MirrorCS"),sQuery(id+"F0.wireOp",EDGE,"E8.MirrorCS"),sQuery(id+"F0.wireOp",EDGE,"E9.MirrorCS"),sQuery(id+"F0.wireOp",EDGE,"E10.MirrorCS"),sQuery(id+"F0.wireOp",EDGE,"E11.MirrorCS"),sQuery(id+"F0.wireOp",EDGE,"E12.MirrorCS"),sQuery(id+"F0.wireOp",EDGE,"E13.MirrorCS"),sQuery(id+"F0.wireOp",EDGE,"E14.MirrorCS"),sQuery(id+"F0.wireOp",EDGE,"E15.MirrorCS"),sQuery(id+"F0.wireOp",EDGE,"E17"),sQuery(id+"F0.wireOp",EDGE,"E18"),sQuery(id+"F0.wireOp",EDGE,"E19"),sQuery(id+"F0.wireOp",EDGE,"E20"),sQuery(id+"F0.wireOp",EDGE,"E21"),sQuery(id+"F0.wireOp",EDGE,"E22"),sQuery(id+"F0.wireOp",EDGE,"E23"),sQuery(id+"F0.wireOp",EDGE,"E24"),sQuery(id+"F0.wireOp",EDGE,"E27.MirrorCS"),sQuery(id+"F0.wireOp",EDGE,"E26.MirrorCS"),sQuery(id+"F0.wireOp",EDGE,"E28.MirrorCS"),sQuery(id+"F0.wireOp",EDGE,"E29.MirrorCS"),sQuery(id+"F0.wireOp",EDGE,"E30.MirrorCS"),sQuery(id+"F0.wireOp",EDGE,"E31.MirrorCS"),sQuery(id+"F0.wireOp",EDGE,"E32.MirrorCS"),sQuery(id+"F0.wireOp",EDGE,"E33.MirrorCS"),sQuery(id+"F0.wireOp",EDGE,"E34.MirrorCS"),sQuery(id+"F0.wireOp",EDGE,"E35.MirrorCS"),sQuery(id+"F0.wireOp",EDGE,"E36.MirrorCS"),sQuery(id+"F0.wireOp",EDGE,"E37.MirrorCS"),sQuery(id+"F0.wireOp",EDGE,"E38.MirrorCS"),sQuery(id+"F0.wireOp",EDGE,"E39.MirrorCS"),sQuery(id+"F0.wireOp",EDGE,"E40.MirrorCS"),sQuery(id+"F0.wireOp",EDGE,"E41.MirrorCS"),sQuery(id+"F0.wireOp",EDGE,"E43.MirrorCS"),sQuery(id+"F0.wireOp",EDGE,"E44.MirrorCS"),sQuery(id+"F0.wireOp",EDGE,"E45.MirrorCS"),sQuery(id+"F0.wireOp",EDGE,"E46.MirrorCS"),sQuery(id+"F0.wireOp",EDGE,"E47.MirrorCS"),sQuery(id+"F0.wireOp",EDGE,"E48.MirrorCS"),sQuery(id+"F0.wireOp",EDGE,"E49.MirrorCS"),sQuery(id+"F0.wireOp",EDGE,"E50.MirrorCS"),sQuery(id+"F0.wireOp",EDGE,"E51.MirrorCS"),sQuery(id+"F0.wireOp",EDGE,"E52.MirrorCS"),sQuery(id+"F0.wireOp",EDGE,"E53.MirrorCS"),sQuery(id+"F0.wireOp",EDGE,"E54"),sQuery(id+"F0.wireOp",EDGE,"E55"),sQuery(id+"F0.wireOp",EDGE,"E61.1.0.0"),sQuery(id+"F0.wireOp",EDGE,"E61.1.0.1"),sQuery(id+"F0.wireOp",EDGE,"E61.1.0.2"),sQuery(id+"F0.wireOp",EDGE,"E61.2.0.0"),sQuery(id+"F0.wireOp",EDGE,"E61.2.0.1"),sQuery(id+"F0.wireOp",EDGE,"E61.2.0.2"),sQuery(id+"F0.wireOp",EDGE,"E61.3.0.0"),sQuery(id+"F0.wireOp",EDGE,"E61.3.0.1"),sQuery(id+"F0.wireOp",EDGE,"E61.3.0.2"),sQuery(id+"F0.wireOp",EDGE,"E61.4.0.0"),sQuery(id+"F0.wireOp",EDGE,"E61.4.0.1"),sQuery(id+"F0.wireOp",EDGE,"E61.4.0.2"),sQuery(id+"F0.wireOp",EDGE,"E61.5.0.0"),sQuery(id+"F0.wireOp",EDGE,"E61.5.0.1"),sQuery(id+"F0.wireOp",EDGE,"E61.5.0.2"),sQuery(id+"F0.wireOp",EDGE,"E62.MirrorCS"),sQuery(id+"F0.wireOp",EDGE,"E64.MirrorCS"),sQuery(id+"F0.wireOp",EDGE,"E65.MirrorCS"),sQuery(id+"F0.wireOp",EDGE,"E66.MirrorCS"),sQuery(id+"F0.wireOp",EDGE,"E67.MirrorCS"),sQuery(id+"F0.wireOp",EDGE,"E68.MirrorCS"),sQuery(id+"F0.wireOp",EDGE,"E69.MirrorCS"),sQuery(id+"F0.wireOp",EDGE,"E70.MirrorCS"),sQuery(id+"F0.wireOp",EDGE,"E59.MirrorCS"),sQuery(id+"F0.wireOp",EDGE,"E58"),sQuery(id+"F0.wireOp",EDGE,"E71.MirrorCS"),sQuery(id+"F0.wireOp",EDGE,"E72.MirrorCS"),sQuery(id+"F0.wireOp",EDGE,"E73.MirrorCS"),sQuery(id+"F0.wireOp",EDGE,"E74.MirrorCS"),sQuery(id+"F0.wireOp",EDGE,"E76.MirrorCS"),sQuery(id+"F0.wireOp",EDGE,"E77.MirrorCS"),sQuery(id+"F0.wireOp",EDGE,"E78.MirrorCS"),sQuery(id+"F0.wireOp",EDGE,"E79.MirrorCS"),sQuery(id+"F0.wireOp",EDGE,"E80"),sQuery(id+"F0.wireOp",EDGE,"E81"),sQuery(id+"F0.wireOp",EDGE,"E82"),sQuery(id+"F0.wireOp",EDGE,"E83"),sQuery(id+"F0.wireOp",EDGE,"E84"),sQuery(id+"F0.wireOp",EDGE,"E85"),sQuery(id+"F0.wireOp",EDGE,"E86"),sQuery(id+"F0.wireOp",EDGE,"E87"),sQuery(id+"F0.wireOp",EDGE,"E88"),sQuery(id+"F0.wireOp",EDGE,"E89"),sQuery(id+"F0.wireOp",EDGE,"E90"),sQuery(id+"F0.wireOp",EDGE,"E91"),sQuery(id+"F0.wireOp",EDGE,"E93.MirrorCS"),sQuery(id+"F0.wireOp",EDGE,"E95.MirrorCS"),sQuery(id+"F0.wireOp",EDGE,"E94.MirrorCS"),sQuery(id+"F0.wireOp",EDGE,"E98.MirrorCS"),sQuery(id+"F0.wireOp",EDGE,"E99.MirrorCS"),sQuery(id+"F0.wireOp",EDGE,"E100.MirrorCS"),sQuery(id+"F0.wireOp",EDGE,"E101.MirrorCS"),sQuery(id+"F0.wireOp",EDGE,"E102.MirrorCS"),sQuery(id+"F0.wireOp",EDGE,"E103.MirrorCS"),sQuery(id+"F0.wireOp",EDGE,"E104.MirrorCS"),sQuery(id+"F0.wireOp",EDGE,"E105.MirrorCS"),sQuery(id+"F0.wireOp",EDGE,"E106.MirrorCS"),sQuery(id+"F0.wireOp",EDGE,"E107.MirrorCS"),sQuery(id+"F0.wireOp",EDGE,"E108.MirrorCS"),sQuery(id+"F0.wireOp",EDGE,"E109.MirrorCS"),sQuery(id+"F0.wireOp",EDGE,"E110.MirrorCS"),sQuery(id+"F0.wireOp",EDGE,"E111.MirrorCS"),sQuery(id+"F0.wireOp",EDGE,"E112.MirrorCS"),sQuery(id+"F0.wireOp",EDGE,"E113.MirrorCS"),sQuery(id+"F0.wireOp",EDGE,"E114.MirrorCS"),sQuery(id+"F0.wireOp",EDGE,"E115.MirrorCS"),sQuery(id+"F0.wireOp",EDGE,"E116.MirrorCS"),sQuery(id+"F0.wireOp",EDGE,"E117.MirrorCS"),sQuery(id+"F0.wireOp",EDGE,"E119.MirrorCS"),sQuery(id+"F0.wireOp",EDGE,"E120.MirrorCS"),sQuery(id+"F0.wireOp",EDGE,"E121.MirrorCS"),sQuery(id+"F0.wireOp",EDGE,"E122.MirrorCS"),sQuery(id+"F0.wireOp",EDGE,"E123.MirrorCS"),sQuery(id+"F0.wireOp",EDGE,"E124.MirrorCS"),sQuery(id+"F0.wireOp",EDGE,"E125.MirrorCS"),sQuery(id+"F0.wireOp",EDGE,"E126.MirrorCS"),sQuery(id+"F0.wireOp",EDGE,"E127.MirrorCS"),sQuery(id+"F0.wireOp",EDGE,"E128.MirrorCS"),sQuery(id+"F0.wireOp",EDGE,"E129.MirrorCS"),sQuery(id+"F0.wireOp",EDGE,"E130.MirrorCS"),sQuery(id+"F0.wireOp",EDGE,"E131.MirrorCS"),sQuery(id+"F0.wireOp",EDGE,"E132.MirrorCS"),sQuery(id+"F0.wireOp",EDGE,"E135.MirrorCS"),sQuery(id+"F0.wireOp",EDGE,"E136.MirrorCS"),sQuery(id+"F0.wireOp",EDGE,"E137.MirrorCS"),sQuery(id+"F0.wireOp",EDGE,"E138.MirrorCS"),sQuery(id+"F0.wireOp",EDGE,"E139.MirrorCS"),sQuery(id+"F0.wireOp",EDGE,"E140.MirrorCS"),sQuery(id+"F0.wireOp",EDGE,"E141.MirrorCS"),sQuery(id+"F0.wireOp",EDGE,"E142.MirrorCS")])],"isStart":true});
            extrude(context, id + "F11", {"entities" : qUnion([Q0]), "endBound" : BoundingType.UP_TO_SURFACE, "oppositeDirection" : true, "endBoundEntityFace" : qUnion([Q1]), "depth" : 25 * mm});
        }
        {
            var Q0;
            Q0=makeQuery(id+"F7.imprint","IMPRINT",FACE,{"disambiguationData":[TD([[makeQuery(id+"F7.imprint","IMPRINT",EDGE,{"derivedFrom":sQuery(id+"F7.wireOp",EDGE,"E160.0.2.0")}),1.0]])]});
            var Q1;
            Q1=makeQuery(id+"F7.imprint","IMPRINT",FACE,{"disambiguationData":[TD([[makeQuery(id+"F7.imprint","IMPRINT",EDGE,{"derivedFrom":sQuery(id+"F7.wireOp",EDGE,"E160.0.1.0")}),1.0]])]});
            var Q2;
            Q2=makeQuery(id+"F7.imprint","IMPRINT",FACE,{"disambiguationData":[TD([[makeQuery(id+"F7.imprint","IMPRINT",EDGE,{"derivedFrom":sQuery(id+"F7.wireOp",EDGE,"E157")}),1.0]])]});
            var Q3;
            Q3=makeQuery(id+"F7.imprint","IMPRINT",FACE,{"disambiguationData":[TD([[makeQuery(id+"F7.imprint","IMPRINT",EDGE,{"derivedFrom":sQuery(id+"F7.wireOp",EDGE,"E163.MirrorCS")}),-1.0]])]});
            var Q4;
            Q4=makeQuery(id+"F7.imprint","IMPRINT",FACE,{"disambiguationData":[TD([[makeQuery(id+"F7.imprint","IMPRINT",EDGE,{"derivedFrom":sQuery(id+"F7.wireOp",EDGE,"E161.MirrorCS")}),-1.0]])]});
            var Q5;
            Q5=makeQuery(id+"F7.imprint","IMPRINT",FACE,{"disambiguationData":[TD([[makeQuery(id+"F7.imprint","IMPRINT",EDGE,{"derivedFrom":sQuery(id+"F7.wireOp",EDGE,"E185.MirrorCS")}),-1.0]])]});
            var Q6;
            Q6=makeQuery(id+"F7.imprint","IMPRINT",FACE,{"disambiguationData":[TD([[makeQuery(id+"F7.imprint","IMPRINT",EDGE,{"derivedFrom":sQuery(id+"F7.wireOp",EDGE,"E180.MirrorCS")}),-1.0]])]});
            var Q7;
            Q7=makeQuery(id+"F7.imprint","IMPRINT",FACE,{"disambiguationData":[TD([[makeQuery(id+"F7.imprint","IMPRINT",EDGE,{"derivedFrom":sQuery(id+"F7.wireOp",EDGE,"E175.MirrorCS")}),-1.0]])]});
            var Q8;
            Q8=makeQuery(id+"F7.imprint","IMPRINT",FACE,{"disambiguationData":[TD([[makeQuery(id+"F7.imprint","IMPRINT",EDGE,{"derivedFrom":sQuery(id+"F7.wireOp",EDGE,"E179.MirrorCS")}),1.0]])]});
            var Q9;
            Q9=makeQuery(id+"F7.imprint","IMPRINT",FACE,{"disambiguationData":[TD([[makeQuery(id+"F7.imprint","IMPRINT",EDGE,{"derivedFrom":sQuery(id+"F7.wireOp",EDGE,"E181.MirrorCS")}),-1.0]])]});
            var Q10;
            Q10=makeQuery(id+"F6.opBoolean","MERGE",FACE,{"derivedFrom":[makeQuery(id+"F3.opExtrude","SWEPT_FACE",FACE,{"disambiguationData":[OSD([sQuery(id+"F2.wireOp",EDGE,"E144")])]}),makeQuery(id+"F3.opExtrude","SWEPT_FACE",FACE,{"disambiguationData":[OSD([sQuery(id+"F2.wireOp",EDGE,"E145")])]}),makeQuery(id+"F3.opExtrude","SWEPT_FACE",FACE,{"disambiguationData":[OSD([sQuery(id+"F2.wireOp",EDGE,"E146")])]}),makeQuery(id+"F3.opExtrude","SWEPT_FACE",FACE,{"disambiguationData":[OSD([sQuery(id+"F2.wireOp",EDGE,"E147")])]}),makeQuery(id+"F3.opExtrude","SWEPT_FACE",FACE,{"disambiguationData":[OSD([sQuery(id+"F2.wireOp",EDGE,"E148")])]}),makeQuery(id+"F3.opExtrude","SWEPT_FACE",FACE,{"disambiguationData":[OSD([sQuery(id+"F2.wireOp",EDGE,"E149")])]}),makeQuery(id+"F3.opExtrude","SWEPT_FACE",FACE,{"disambiguationData":[OSD([sQuery(id+"F2.wireOp",EDGE,"E150")])]}),makeQuery(id+"F5.opExtrude","SWEPT_FACE",FACE,{"disambiguationData":[OSD([sQuery(id+"F4.wireOp",EDGE,"E154.left")])]})]});
            extrude(context, id + "F12", {"entities" : qUnion([Q0, Q1, Q2, Q3, Q4, Q5, Q6, Q7, Q8, Q9]), "endBound" : BoundingType.UP_TO_SURFACE, "oppositeDirection" : true, "endBoundEntityFace" : qUnion([Q10]), "depth" : 25 * mm});
        }
        {
            var Q0;
            Q0=makeQuery(id+"F9.opPattern","COPY",FACE,{"derivedFrom":makeQuery(id+"F6.opBoolean","MERGE",FACE,{"derivedFrom":[makeQuery(id+"F3.opExtrude","SWEPT_FACE",FACE,{"disambiguationData":[OSD([sQuery(id+"F2.wireOp",EDGE,"E143.0.59")])]}),makeQuery(id+"F3.opExtrude","SWEPT_FACE",FACE,{"disambiguationData":[OSD([sQuery(id+"F2.wireOp",EDGE,"E143.0.63")])]}),makeQuery(id+"F3.opExtrude","SWEPT_FACE",FACE,{"disambiguationData":[OSD([sQuery(id+"F2.wireOp",EDGE,"E143.0.67")])]}),makeQuery(id+"F3.opExtrude","SWEPT_FACE",FACE,{"disambiguationData":[OSD([sQuery(id+"F2.wireOp",EDGE,"E143.0.71")])]}),makeQuery(id+"F3.opExtrude","SWEPT_FACE",FACE,{"disambiguationData":[OSD([sQuery(id+"F2.wireOp",EDGE,"E143.0.75")])]}),makeQuery(id+"F3.opExtrude","SWEPT_FACE",FACE,{"disambiguationData":[OSD([sQuery(id+"F2.wireOp",EDGE,"E143.0.79")])]}),makeQuery(id+"F3.opExtrude","SWEPT_FACE",FACE,{"disambiguationData":[OSD([sQuery(id+"F2.wireOp",EDGE,"E143.0.83")])]}),makeQuery(id+"F5.opExtrude","SWEPT_FACE",FACE,{"disambiguationData":[OSD([sQuery(id+"F4.wireOp",EDGE,"E154.right")])]})]}),"instanceName":"1"});
            var sketch = newSketch(context, id + "F13", { "sketchPlane" : qUnion([Q0])});
            skLineSegment(sketch, "E207.0", {"start": v(-96, 89) * mm, "end": v(-100, 89) * mm});
            skLineSegment(sketch, "E207.1", {"start": v(-96, 29) * mm, "end": v(-100, 29) * mm});
            skLineSegment(sketch, "E207.2", {"start": v(-96, 49) * mm, "end": v(-100, 49) * mm});
            skLineSegment(sketch, "E207.3", {"start": v(-100, 89) * mm, "end": v(-100, 79) * mm});
            skLineSegment(sketch, "E207.4", {"start": v(-96, 9) * mm, "end": v(-100, 9) * mm});
            skLineSegment(sketch, "E207.5", {"start": v(-96, 69) * mm, "end": v(-100, 69) * mm});
            skLineSegment(sketch, "E207.6", {"start": v(-96, 89) * mm, "end": v(-100, 89) * mm});
            skLineSegment(sketch, "E207.7", {"start": v(-100, 49) * mm, "end": v(-100, 39) * mm});
            skLineSegment(sketch, "E207.8", {"start": v(-96, 19) * mm, "end": v(-96, 9) * mm});
            skLineSegment(sketch, "E207.9", {"start": v(-96, 39) * mm, "end": v(-96, 29) * mm});
            skLineSegment(sketch, "E207.10", {"start": v(-96, 49) * mm, "end": v(-100, 49) * mm});
            skLineSegment(sketch, "E207.15", {"start": v(-96, 69) * mm, "end": v(-96, 79) * mm});
            skLineSegment(sketch, "E207.16", {"start": v(-96, 99) * mm, "end": v(-100, 99) * mm});
            skLineSegment(sketch, "E207.17", {"start": v(-96, 29) * mm, "end": v(-100, 29) * mm});
            skLineSegment(sketch, "E207.18", {"start": v(-96, 79) * mm, "end": v(-100, 79) * mm});
            skLineSegment(sketch, "E207.20", {"start": v(-96, 69) * mm, "end": v(-100, 69) * mm});
            skLineSegment(sketch, "E207.21", {"start": v(-96, 49) * mm, "end": v(-96, 59) * mm});
            skLineSegment(sketch, "E207.23", {"start": v(-96, 39) * mm, "end": v(-100, 39) * mm});
            skLineSegment(sketch, "E207.24", {"start": v(-100, 29) * mm, "end": v(-100, 19) * mm});
            skLineSegment(sketch, "E207.25", {"start": v(-96, 99) * mm, "end": v(-100, 99) * mm});
            skLineSegment(sketch, "E207.28", {"start": v(-96, 19) * mm, "end": v(-100, 19) * mm});
            skLineSegment(sketch, "E207.29", {"start": v(-96, 39) * mm, "end": v(-96, 29) * mm});
            skLineSegment(sketch, "E207.30", {"start": v(-100, 69) * mm, "end": v(-100, 59) * mm});
            skLineSegment(sketch, "E207.31", {"start": v(-96, 19) * mm, "end": v(-100, 19) * mm});
            skLineSegment(sketch, "E207.32", {"start": v(-96, 89) * mm, "end": v(-96, 99) * mm});
            skLineSegment(sketch, "E207.33", {"start": v(-96, 39) * mm, "end": v(-100, 39) * mm});
            skLineSegment(sketch, "E207.37", {"start": v(-96, 79) * mm, "end": v(-100, 79) * mm});
            skLineSegment(sketch, "E207.38", {"start": v(-96, 59) * mm, "end": v(-100, 59) * mm});
            skLineSegment(sketch, "E207.39", {"start": v(-96, 9) * mm, "end": v(-100, 9) * mm});
            skLineSegment(sketch, "E207.43", {"start": v(-96, 59) * mm, "end": v(-100, 59) * mm});
            skLineSegment(sketch, "E207.45", {"start": v(-100, 89) * mm, "end": v(-100, 79) * mm});
            skLineSegment(sketch, "E207.46", {"start": v(-100, 49) * mm, "end": v(-100, 39) * mm});
            skLineSegment(sketch, "E207.47", {"start": v(-96, 19) * mm, "end": v(-96, 9) * mm});
            skLineSegment(sketch, "E207.48", {"start": v(-96, 49) * mm, "end": v(-96, 59) * mm});
            skLineSegment(sketch, "E207.49", {"start": v(-96, 69) * mm, "end": v(-96, 79) * mm});
            skLineSegment(sketch, "E207.51", {"start": v(-100, 29) * mm, "end": v(-100, 19) * mm});
            skLineSegment(sketch, "E207.53", {"start": v(-100, 69) * mm, "end": v(-100, 59) * mm});
            skLineSegment(sketch, "E207.55", {"start": v(-96, 89) * mm, "end": v(-96, 99) * mm});
            skLineSegment(sketch, "E208.0", {"start": v(96, 69) * mm, "end": v(96, 79) * mm});
            skLineSegment(sketch, "E208.1", {"start": v(96, 89) * mm, "end": v(96, 99) * mm});
            skLineSegment(sketch, "E208.2", {"start": v(96, 59) * mm, "end": v(100, 59) * mm});
            skLineSegment(sketch, "E208.3", {"start": v(96, 79) * mm, "end": v(100, 79) * mm});
            skLineSegment(sketch, "E208.4", {"start": v(96, 39) * mm, "end": v(100, 39) * mm});
            skLineSegment(sketch, "E208.5", {"start": v(96, 99) * mm, "end": v(100, 99) * mm});
            skLineSegment(sketch, "E208.6", {"start": v(100, 89) * mm, "end": v(100, 79) * mm});
            skLineSegment(sketch, "E208.7", {"start": v(96, 49) * mm, "end": v(96, 59) * mm});
            skLineSegment(sketch, "E208.8", {"start": v(96, 19) * mm, "end": v(100, 19) * mm});
            skLineSegment(sketch, "E208.9", {"start": v(96, 9) * mm, "end": v(100, 9) * mm});
            skLineSegment(sketch, "E208.10", {"start": v(100, 49) * mm, "end": v(100, 39) * mm});
            skLineSegment(sketch, "E208.11", {"start": v(96, 39) * mm, "end": v(96, 29) * mm});
            skLineSegment(sketch, "E208.12", {"start": v(96, 59) * mm, "end": v(100, 59) * mm});
            skLineSegment(sketch, "E208.13", {"start": v(96, 69) * mm, "end": v(100, 69) * mm});
            skLineSegment(sketch, "E208.14", {"start": v(96, 29) * mm, "end": v(100, 29) * mm});
            skLineSegment(sketch, "E208.15", {"start": v(96, 39) * mm, "end": v(100, 39) * mm});
            skLineSegment(sketch, "E208.16", {"start": v(96, 19) * mm, "end": v(96, 9) * mm});
            skLineSegment(sketch, "E208.18", {"start": v(100, 29) * mm, "end": v(100, 19) * mm});
            skLineSegment(sketch, "E208.20", {"start": v(96, 19) * mm, "end": v(100, 19) * mm});
            skLineSegment(sketch, "E208.21", {"start": v(100, 69) * mm, "end": v(100, 59) * mm});
            skLineSegment(sketch, "E208.22", {"start": v(96, 9) * mm, "end": v(100, 9) * mm});
            skLineSegment(sketch, "E208.23", {"start": v(100, 29) * mm, "end": v(100, 19) * mm});
            skLineSegment(sketch, "E208.27", {"start": v(96, 89) * mm, "end": v(100, 89) * mm});
            skLineSegment(sketch, "E208.29", {"start": v(96, 69) * mm, "end": v(100, 69) * mm});
            skLineSegment(sketch, "E208.30", {"start": v(96, 49) * mm, "end": v(100, 49) * mm});
            skLineSegment(sketch, "E208.31", {"start": v(100, 49) * mm, "end": v(100, 39) * mm});
            skLineSegment(sketch, "E208.33", {"start": v(96, 49) * mm, "end": v(100, 49) * mm});
            skLineSegment(sketch, "E208.37", {"start": v(96, 89) * mm, "end": v(100, 89) * mm});
            skLineSegment(sketch, "E208.38", {"start": v(96, 29) * mm, "end": v(100, 29) * mm});
            skLineSegment(sketch, "E208.39", {"start": v(96, 79) * mm, "end": v(100, 79) * mm});
            skLineSegment(sketch, "E208.42", {"start": v(96, 49) * mm, "end": v(96, 59) * mm});
            skLineSegment(sketch, "E208.43", {"start": v(100, 89) * mm, "end": v(100, 79) * mm});
            skLineSegment(sketch, "E208.45", {"start": v(96, 19) * mm, "end": v(96, 9) * mm});
            skLineSegment(sketch, "E208.46", {"start": v(100, 69) * mm, "end": v(100, 59) * mm});
            skLineSegment(sketch, "E208.51", {"start": v(96, 39) * mm, "end": v(96, 29) * mm});
            skLineSegment(sketch, "E208.53", {"start": v(96, 69) * mm, "end": v(96, 79) * mm});
            skLineSegment(sketch, "E209", {"start": v(-100, 99) * mm, "end": v(-100, 9) * mm});
            skLineSegment(sketch, "E210", {"start": v(100, 99) * mm, "end": v(100, 9) * mm});
            skSolve(sketch);
        }
        {
            var Q0;
            Q0 = qSketchRegion(id + "F13", true);
            var Q1;
            Q1=makeQuery(id+"F9.opPattern","COPY",FACE,{"derivedFrom":makeQuery(id+"F6.opBoolean","MERGE",FACE,{"derivedFrom":[makeQuery(id+"F3.opExtrude","SWEPT_FACE",FACE,{"disambiguationData":[OSD([sQuery(id+"F2.wireOp",EDGE,"E144")])]}),makeQuery(id+"F3.opExtrude","SWEPT_FACE",FACE,{"disambiguationData":[OSD([sQuery(id+"F2.wireOp",EDGE,"E145")])]}),makeQuery(id+"F3.opExtrude","SWEPT_FACE",FACE,{"disambiguationData":[OSD([sQuery(id+"F2.wireOp",EDGE,"E146")])]}),makeQuery(id+"F3.opExtrude","SWEPT_FACE",FACE,{"disambiguationData":[OSD([sQuery(id+"F2.wireOp",EDGE,"E147")])]}),makeQuery(id+"F3.opExtrude","SWEPT_FACE",FACE,{"disambiguationData":[OSD([sQuery(id+"F2.wireOp",EDGE,"E148")])]}),makeQuery(id+"F3.opExtrude","SWEPT_FACE",FACE,{"disambiguationData":[OSD([sQuery(id+"F2.wireOp",EDGE,"E149")])]}),makeQuery(id+"F3.opExtrude","SWEPT_FACE",FACE,{"disambiguationData":[OSD([sQuery(id+"F2.wireOp",EDGE,"E150")])]}),makeQuery(id+"F5.opExtrude","SWEPT_FACE",FACE,{"disambiguationData":[OSD([sQuery(id+"F4.wireOp",EDGE,"E154.left")])]})]}),"instanceName":"1"});
            extrude(context, id + "F14", {"entities" : qUnion([Q0]), "endBound" : BoundingType.UP_TO_SURFACE, "oppositeDirection" : true, "endBoundEntityFace" : qUnion([Q1]), "depth" : 25 * mm});
        }
        {
            var Q0;
            Q0=makeQuery(id+"F1.opExtrude","CAP_FACE",FACE,{"disambiguationData":[OSD([sQuery(id+"F0.wireOp",EDGE,"E2"),sQuery(id+"F0.wireOp",EDGE,"E4"),sQuery(id+"F0.wireOp",EDGE,"E6.0.1.0"),sQuery(id+"F0.wireOp",EDGE,"E6.0.1.1"),sQuery(id+"F0.wireOp",EDGE,"E6.0.1.2"),sQuery(id+"F0.wireOp",EDGE,"E6.0.2.0"),sQuery(id+"F0.wireOp",EDGE,"E6.0.2.1"),sQuery(id+"F0.wireOp",EDGE,"E6.0.2.2"),sQuery(id+"F0.wireOp",EDGE,"E6.0.3.0"),sQuery(id+"F0.wireOp",EDGE,"E6.0.3.1"),sQuery(id+"F0.wireOp",EDGE,"E6.0.3.2"),sQuery(id+"F0.wireOp",EDGE,"E7.MirrorCS"),sQuery(id+"F0.wireOp",EDGE,"E3.MirrorCS"),sQuery(id+"F0.wireOp",EDGE,"E8.MirrorCS"),sQuery(id+"F0.wireOp",EDGE,"E9.MirrorCS"),sQuery(id+"F0.wireOp",EDGE,"E10.MirrorCS"),sQuery(id+"F0.wireOp",EDGE,"E11.MirrorCS"),sQuery(id+"F0.wireOp",EDGE,"E12.MirrorCS"),sQuery(id+"F0.wireOp",EDGE,"E13.MirrorCS"),sQuery(id+"F0.wireOp",EDGE,"E14.MirrorCS"),sQuery(id+"F0.wireOp",EDGE,"E15.MirrorCS"),sQuery(id+"F0.wireOp",EDGE,"E17"),sQuery(id+"F0.wireOp",EDGE,"E18"),sQuery(id+"F0.wireOp",EDGE,"E19"),sQuery(id+"F0.wireOp",EDGE,"E20"),sQuery(id+"F0.wireOp",EDGE,"E21"),sQuery(id+"F0.wireOp",EDGE,"E22"),sQuery(id+"F0.wireOp",EDGE,"E23"),sQuery(id+"F0.wireOp",EDGE,"E24"),sQuery(id+"F0.wireOp",EDGE,"E27.MirrorCS"),sQuery(id+"F0.wireOp",EDGE,"E26.MirrorCS"),sQuery(id+"F0.wireOp",EDGE,"E28.MirrorCS"),sQuery(id+"F0.wireOp",EDGE,"E29.MirrorCS"),sQuery(id+"F0.wireOp",EDGE,"E30.MirrorCS"),sQuery(id+"F0.wireOp",EDGE,"E31.MirrorCS"),sQuery(id+"F0.wireOp",EDGE,"E32.MirrorCS"),sQuery(id+"F0.wireOp",EDGE,"E33.MirrorCS"),sQuery(id+"F0.wireOp",EDGE,"E34.MirrorCS"),sQuery(id+"F0.wireOp",EDGE,"E35.MirrorCS"),sQuery(id+"F0.wireOp",EDGE,"E36.MirrorCS"),sQuery(id+"F0.wireOp",EDGE,"E37.MirrorCS"),sQuery(id+"F0.wireOp",EDGE,"E38.MirrorCS"),sQuery(id+"F0.wireOp",EDGE,"E39.MirrorCS"),sQuery(id+"F0.wireOp",EDGE,"E40.MirrorCS"),sQuery(id+"F0.wireOp",EDGE,"E41.MirrorCS"),sQuery(id+"F0.wireOp",EDGE,"E43.MirrorCS"),sQuery(id+"F0.wireOp",EDGE,"E44.MirrorCS"),sQuery(id+"F0.wireOp",EDGE,"E45.MirrorCS"),sQuery(id+"F0.wireOp",EDGE,"E46.MirrorCS"),sQuery(id+"F0.wireOp",EDGE,"E47.MirrorCS"),sQuery(id+"F0.wireOp",EDGE,"E48.MirrorCS"),sQuery(id+"F0.wireOp",EDGE,"E49.MirrorCS"),sQuery(id+"F0.wireOp",EDGE,"E50.MirrorCS"),sQuery(id+"F0.wireOp",EDGE,"E51.MirrorCS"),sQuery(id+"F0.wireOp",EDGE,"E52.MirrorCS"),sQuery(id+"F0.wireOp",EDGE,"E53.MirrorCS"),sQuery(id+"F0.wireOp",EDGE,"E54"),sQuery(id+"F0.wireOp",EDGE,"E55"),sQuery(id+"F0.wireOp",EDGE,"E61.1.0.0"),sQuery(id+"F0.wireOp",EDGE,"E61.1.0.1"),sQuery(id+"F0.wireOp",EDGE,"E61.1.0.2"),sQuery(id+"F0.wireOp",EDGE,"E61.2.0.0"),sQuery(id+"F0.wireOp",EDGE,"E61.2.0.1"),sQuery(id+"F0.wireOp",EDGE,"E61.2.0.2"),sQuery(id+"F0.wireOp",EDGE,"E61.3.0.0"),sQuery(id+"F0.wireOp",EDGE,"E61.3.0.1"),sQuery(id+"F0.wireOp",EDGE,"E61.3.0.2"),sQuery(id+"F0.wireOp",EDGE,"E61.4.0.0"),sQuery(id+"F0.wireOp",EDGE,"E61.4.0.1"),sQuery(id+"F0.wireOp",EDGE,"E61.4.0.2"),sQuery(id+"F0.wireOp",EDGE,"E61.5.0.0"),sQuery(id+"F0.wireOp",EDGE,"E61.5.0.1"),sQuery(id+"F0.wireOp",EDGE,"E61.5.0.2"),sQuery(id+"F0.wireOp",EDGE,"E62.MirrorCS"),sQuery(id+"F0.wireOp",EDGE,"E64.MirrorCS"),sQuery(id+"F0.wireOp",EDGE,"E65.MirrorCS"),sQuery(id+"F0.wireOp",EDGE,"E66.MirrorCS"),sQuery(id+"F0.wireOp",EDGE,"E67.MirrorCS"),sQuery(id+"F0.wireOp",EDGE,"E68.MirrorCS"),sQuery(id+"F0.wireOp",EDGE,"E69.MirrorCS"),sQuery(id+"F0.wireOp",EDGE,"E70.MirrorCS"),sQuery(id+"F0.wireOp",EDGE,"E59.MirrorCS"),sQuery(id+"F0.wireOp",EDGE,"E58"),sQuery(id+"F0.wireOp",EDGE,"E71.MirrorCS"),sQuery(id+"F0.wireOp",EDGE,"E72.MirrorCS"),sQuery(id+"F0.wireOp",EDGE,"E73.MirrorCS"),sQuery(id+"F0.wireOp",EDGE,"E74.MirrorCS"),sQuery(id+"F0.wireOp",EDGE,"E76.MirrorCS"),sQuery(id+"F0.wireOp",EDGE,"E77.MirrorCS"),sQuery(id+"F0.wireOp",EDGE,"E78.MirrorCS"),sQuery(id+"F0.wireOp",EDGE,"E79.MirrorCS"),sQuery(id+"F0.wireOp",EDGE,"E80"),sQuery(id+"F0.wireOp",EDGE,"E81"),sQuery(id+"F0.wireOp",EDGE,"E82"),sQuery(id+"F0.wireOp",EDGE,"E83"),sQuery(id+"F0.wireOp",EDGE,"E84"),sQuery(id+"F0.wireOp",EDGE,"E85"),sQuery(id+"F0.wireOp",EDGE,"E86"),sQuery(id+"F0.wireOp",EDGE,"E87"),sQuery(id+"F0.wireOp",EDGE,"E88"),sQuery(id+"F0.wireOp",EDGE,"E89"),sQuery(id+"F0.wireOp",EDGE,"E90"),sQuery(id+"F0.wireOp",EDGE,"E91"),sQuery(id+"F0.wireOp",EDGE,"E93.MirrorCS"),sQuery(id+"F0.wireOp",EDGE,"E95.MirrorCS"),sQuery(id+"F0.wireOp",EDGE,"E94.MirrorCS"),sQuery(id+"F0.wireOp",EDGE,"E98.MirrorCS"),sQuery(id+"F0.wireOp",EDGE,"E99.MirrorCS"),sQuery(id+"F0.wireOp",EDGE,"E100.MirrorCS"),sQuery(id+"F0.wireOp",EDGE,"E101.MirrorCS"),sQuery(id+"F0.wireOp",EDGE,"E102.MirrorCS"),sQuery(id+"F0.wireOp",EDGE,"E103.MirrorCS"),sQuery(id+"F0.wireOp",EDGE,"E104.MirrorCS"),sQuery(id+"F0.wireOp",EDGE,"E105.MirrorCS"),sQuery(id+"F0.wireOp",EDGE,"E106.MirrorCS"),sQuery(id+"F0.wireOp",EDGE,"E107.MirrorCS"),sQuery(id+"F0.wireOp",EDGE,"E108.MirrorCS"),sQuery(id+"F0.wireOp",EDGE,"E109.MirrorCS"),sQuery(id+"F0.wireOp",EDGE,"E110.MirrorCS"),sQuery(id+"F0.wireOp",EDGE,"E111.MirrorCS"),sQuery(id+"F0.wireOp",EDGE,"E112.MirrorCS"),sQuery(id+"F0.wireOp",EDGE,"E113.MirrorCS"),sQuery(id+"F0.wireOp",EDGE,"E114.MirrorCS"),sQuery(id+"F0.wireOp",EDGE,"E115.MirrorCS"),sQuery(id+"F0.wireOp",EDGE,"E116.MirrorCS"),sQuery(id+"F0.wireOp",EDGE,"E117.MirrorCS"),sQuery(id+"F0.wireOp",EDGE,"E119.MirrorCS"),sQuery(id+"F0.wireOp",EDGE,"E120.MirrorCS"),sQuery(id+"F0.wireOp",EDGE,"E121.MirrorCS"),sQuery(id+"F0.wireOp",EDGE,"E122.MirrorCS"),sQuery(id+"F0.wireOp",EDGE,"E123.MirrorCS"),sQuery(id+"F0.wireOp",EDGE,"E124.MirrorCS"),sQuery(id+"F0.wireOp",EDGE,"E125.MirrorCS"),sQuery(id+"F0.wireOp",EDGE,"E126.MirrorCS"),sQuery(id+"F0.wireOp",EDGE,"E127.MirrorCS"),sQuery(id+"F0.wireOp",EDGE,"E128.MirrorCS"),sQuery(id+"F0.wireOp",EDGE,"E129.MirrorCS"),sQuery(id+"F0.wireOp",EDGE,"E130.MirrorCS"),sQuery(id+"F0.wireOp",EDGE,"E131.MirrorCS"),sQuery(id+"F0.wireOp",EDGE,"E132.MirrorCS"),sQuery(id+"F0.wireOp",EDGE,"E135.MirrorCS"),sQuery(id+"F0.wireOp",EDGE,"E136.MirrorCS"),sQuery(id+"F0.wireOp",EDGE,"E137.MirrorCS"),sQuery(id+"F0.wireOp",EDGE,"E138.MirrorCS"),sQuery(id+"F0.wireOp",EDGE,"E139.MirrorCS"),sQuery(id+"F0.wireOp",EDGE,"E140.MirrorCS"),sQuery(id+"F0.wireOp",EDGE,"E141.MirrorCS"),sQuery(id+"F0.wireOp",EDGE,"E142.MirrorCS")])],"isStart":false});
            var sketch = newSketch(context, id + "F15", { "sketchPlane" : qUnion([Q0])});
            skPoint(sketch, "E211.0", {"position": v(-146, 100) * mm});
            skPoint(sketch, "E212.0", {"position": v(130, 96) * mm});
            skLineSegment(sketch, "E213.0", {"start": v(146, 100) * mm, "end": v(146, -100) * mm});
            skLineSegment(sketch, "E214.bottom", {"start": v(-146, 100) * mm, "end": v(146, 100) * mm});
            skLineSegment(sketch, "E214.top", {"start": v(-146, 96) * mm, "end": v(146, 96) * mm});
            skLineSegment(sketch, "E214.left", {"start": v(-146, 100) * mm, "end": v(-146, 96) * mm});
            skLineSegment(sketch, "E214.right", {"start": v(146, 100) * mm, "end": v(146, 96) * mm});
            skPoint(sketch, "E215.0", {"position": v(-146, -100) * mm});
            skPoint(sketch, "E216.0", {"position": v(130, -96) * mm});
            skLineSegment(sketch, "E217.0.1", {"start": v(146, -100) * mm, "end": v(150, -100) * mm});
            skLineSegment(sketch, "E217.0.2", {"start": v(150, -100) * mm, "end": v(150, 100) * mm});
            skLineSegment(sketch, "E217.0.3", {"start": v(150, 100) * mm, "end": v(146, 100) * mm});
            skLineSegment(sketch, "E218.bottom", {"start": v(-146, -100) * mm, "end": v(146, -100) * mm});
            skLineSegment(sketch, "E218.top", {"start": v(-146, -96) * mm, "end": v(146, -96) * mm});
            skLineSegment(sketch, "E218.left", {"start": v(-146, -100) * mm, "end": v(-146, -96) * mm});
            skLineSegment(sketch, "E218.right", {"start": v(146, -100) * mm, "end": v(146, -96) * mm});
            skSolve(sketch);
        }
        {
            var Q0;
            {var subQ1=makeQuery(id+"F1.opExtrude","CAP_EDGE",EDGE,{"disambiguationData":[OSD([sQuery(id+"F0.wireOp",EDGE,"E61.4.0.1")])],"isStart":false});Q0=makeQuery(id+"F15.imprint","IMPRINT",FACE,{"disambiguationData":[TD([[makeQuery(id+"F15.imprint","IMPRINT",EDGE,{"derivedFrom":subQ1}),-1.0]])]});}
            var Q1;
            {var subQ1=makeQuery(id+"F1.opExtrude","CAP_EDGE",EDGE,{"disambiguationData":[OSD([sQuery(id+"F0.wireOp",EDGE,"E61.5.0.1")])],"isStart":false});Q1=makeQuery(id+"F15.imprint","IMPRINT",FACE,{"disambiguationData":[TD([[makeQuery(id+"F15.imprint","IMPRINT",EDGE,{"derivedFrom":subQ1}),-1.0]])]});}
            var Q2;
            {var subQ1=makeQuery(id+"F1.opExtrude","CAP_EDGE",EDGE,{"disambiguationData":[OSD([sQuery(id+"F0.wireOp",EDGE,"E61.5.0.0")])],"isStart":false});Q2=makeQuery(id+"F15.imprint","IMPRINT",FACE,{"disambiguationData":[TD([[makeQuery(id+"F15.imprint","IMPRINT",EDGE,{"derivedFrom":subQ1}),-1.0]])]});}
            var Q3;
            {var subQ1=makeQuery(id+"F1.opExtrude","CAP_EDGE",EDGE,{"disambiguationData":[OSD([sQuery(id+"F0.wireOp",EDGE,"E61.4.0.0")])],"isStart":false});Q3=makeQuery(id+"F15.imprint","IMPRINT",FACE,{"disambiguationData":[TD([[makeQuery(id+"F15.imprint","IMPRINT",EDGE,{"derivedFrom":subQ1}),-1.0]])]});}
            var Q4;
            {var subQ1=makeQuery(id+"F1.opExtrude","CAP_EDGE",EDGE,{"disambiguationData":[OSD([sQuery(id+"F0.wireOp",EDGE,"E61.3.0.1")])],"isStart":false});Q4=makeQuery(id+"F15.imprint","IMPRINT",FACE,{"disambiguationData":[TD([[makeQuery(id+"F15.imprint","IMPRINT",EDGE,{"derivedFrom":subQ1}),-1.0]])]});}
            var Q5;
            {var subQ1=makeQuery(id+"F1.opExtrude","CAP_EDGE",EDGE,{"disambiguationData":[OSD([sQuery(id+"F0.wireOp",EDGE,"E61.3.0.0")])],"isStart":false});Q5=makeQuery(id+"F15.imprint","IMPRINT",FACE,{"disambiguationData":[TD([[makeQuery(id+"F15.imprint","IMPRINT",EDGE,{"derivedFrom":subQ1}),-1.0]])]});}
            var Q6;
            {var subQ1=makeQuery(id+"F1.opExtrude","CAP_EDGE",EDGE,{"disambiguationData":[OSD([sQuery(id+"F0.wireOp",EDGE,"E61.2.0.1")])],"isStart":false});Q6=makeQuery(id+"F15.imprint","IMPRINT",FACE,{"disambiguationData":[TD([[makeQuery(id+"F15.imprint","IMPRINT",EDGE,{"derivedFrom":subQ1}),-1.0]])]});}
            var Q7;
            {var subQ1=makeQuery(id+"F1.opExtrude","CAP_EDGE",EDGE,{"disambiguationData":[OSD([sQuery(id+"F0.wireOp",EDGE,"E61.2.0.0")])],"isStart":false});Q7=makeQuery(id+"F15.imprint","IMPRINT",FACE,{"disambiguationData":[TD([[makeQuery(id+"F15.imprint","IMPRINT",EDGE,{"derivedFrom":subQ1}),-1.0]])]});}
            var Q8;
            {var subQ1=makeQuery(id+"F1.opExtrude","CAP_EDGE",EDGE,{"disambiguationData":[OSD([sQuery(id+"F0.wireOp",EDGE,"E61.1.0.1")])],"isStart":false});Q8=makeQuery(id+"F15.imprint","IMPRINT",FACE,{"disambiguationData":[TD([[makeQuery(id+"F15.imprint","IMPRINT",EDGE,{"derivedFrom":subQ1}),-1.0]])]});}
            var Q9;
            {var subQ1=makeQuery(id+"F1.opExtrude","CAP_EDGE",EDGE,{"disambiguationData":[OSD([sQuery(id+"F0.wireOp",EDGE,"E61.1.0.0")])],"isStart":false});Q9=makeQuery(id+"F15.imprint","IMPRINT",FACE,{"disambiguationData":[TD([[makeQuery(id+"F15.imprint","IMPRINT",EDGE,{"derivedFrom":subQ1}),-1.0]])]});}
            var Q10;
            {var subQ1=makeQuery(id+"F1.opExtrude","CAP_EDGE",EDGE,{"disambiguationData":[OSD([sQuery(id+"F0.wireOp",EDGE,"E61.1.0.0")])],"isStart":false});Q10=makeQuery(id+"F15.imprint","IMPRINT",FACE,{"disambiguationData":[TD([[makeQuery(id+"F15.imprint","IMPRINT",EDGE,{"derivedFrom":subQ1}),1.0]])]});}
            var Q11;
            {var subQ1=makeQuery(id+"F1.opExtrude","CAP_EDGE",EDGE,{"disambiguationData":[OSD([sQuery(id+"F0.wireOp",EDGE,"E59.MirrorCS")])],"isStart":false});Q11=makeQuery(id+"F15.imprint","IMPRINT",FACE,{"disambiguationData":[TD([[makeQuery(id+"F15.imprint","IMPRINT",EDGE,{"derivedFrom":subQ1}),-1.0]])]});}
            var Q12;
            {var subQ1=makeQuery(id+"F1.opExtrude","CAP_EDGE",EDGE,{"disambiguationData":[OSD([sQuery(id+"F0.wireOp",EDGE,"E65.MirrorCS")])],"isStart":false});Q12=makeQuery(id+"F15.imprint","IMPRINT",FACE,{"disambiguationData":[TD([[makeQuery(id+"F15.imprint","IMPRINT",EDGE,{"derivedFrom":subQ1}),-1.0]])]});}
            var Q13;
            {var subQ1=makeQuery(id+"F1.opExtrude","CAP_EDGE",EDGE,{"disambiguationData":[OSD([sQuery(id+"F0.wireOp",EDGE,"E65.MirrorCS")])],"isStart":false});Q13=makeQuery(id+"F15.imprint","IMPRINT",FACE,{"disambiguationData":[TD([[makeQuery(id+"F15.imprint","IMPRINT",EDGE,{"derivedFrom":subQ1}),1.0]])]});}
            var Q14;
            {var subQ1=makeQuery(id+"F1.opExtrude","CAP_EDGE",EDGE,{"disambiguationData":[OSD([sQuery(id+"F0.wireOp",EDGE,"E68.MirrorCS")])],"isStart":false});Q14=makeQuery(id+"F15.imprint","IMPRINT",FACE,{"disambiguationData":[TD([[makeQuery(id+"F15.imprint","IMPRINT",EDGE,{"derivedFrom":subQ1}),-1.0]])]});}
            var Q15;
            {var subQ1=makeQuery(id+"F1.opExtrude","CAP_EDGE",EDGE,{"disambiguationData":[OSD([sQuery(id+"F0.wireOp",EDGE,"E68.MirrorCS")])],"isStart":false});Q15=makeQuery(id+"F15.imprint","IMPRINT",FACE,{"disambiguationData":[TD([[makeQuery(id+"F15.imprint","IMPRINT",EDGE,{"derivedFrom":subQ1}),1.0]])]});}
            var Q16;
            {var subQ1=makeQuery(id+"F1.opExtrude","CAP_EDGE",EDGE,{"disambiguationData":[OSD([sQuery(id+"F0.wireOp",EDGE,"E70.MirrorCS")])],"isStart":false});Q16=makeQuery(id+"F15.imprint","IMPRINT",FACE,{"disambiguationData":[TD([[makeQuery(id+"F15.imprint","IMPRINT",EDGE,{"derivedFrom":subQ1}),-1.0]])]});}
            var Q17;
            {var subQ1=makeQuery(id+"F1.opExtrude","CAP_EDGE",EDGE,{"disambiguationData":[OSD([sQuery(id+"F0.wireOp",EDGE,"E71.MirrorCS")])],"isStart":false});Q17=makeQuery(id+"F15.imprint","IMPRINT",FACE,{"disambiguationData":[TD([[makeQuery(id+"F15.imprint","IMPRINT",EDGE,{"derivedFrom":subQ1}),1.0]])]});}
            var Q18;
            {var subQ1=makeQuery(id+"F1.opExtrude","CAP_EDGE",EDGE,{"disambiguationData":[OSD([sQuery(id+"F0.wireOp",EDGE,"E64.MirrorCS")])],"isStart":false});Q18=makeQuery(id+"F15.imprint","IMPRINT",FACE,{"disambiguationData":[TD([[makeQuery(id+"F15.imprint","IMPRINT",EDGE,{"derivedFrom":subQ1}),-1.0]])]});}
            var Q19;
            {var subQ1=makeQuery(id+"F1.opExtrude","CAP_EDGE",EDGE,{"disambiguationData":[OSD([sQuery(id+"F0.wireOp",EDGE,"E64.MirrorCS")])],"isStart":false});Q19=makeQuery(id+"F15.imprint","IMPRINT",FACE,{"disambiguationData":[TD([[makeQuery(id+"F15.imprint","IMPRINT",EDGE,{"derivedFrom":subQ1}),1.0]])]});}
            var Q20;
            {var subQ1=makeQuery(id+"F1.opExtrude","CAP_EDGE",EDGE,{"disambiguationData":[OSD([sQuery(id+"F0.wireOp",EDGE,"E66.MirrorCS")])],"isStart":false});Q20=makeQuery(id+"F15.imprint","IMPRINT",FACE,{"disambiguationData":[TD([[makeQuery(id+"F15.imprint","IMPRINT",EDGE,{"derivedFrom":subQ1}),-1.0]])]});}
            var Q21;
            {var subQ1=makeQuery(id+"F1.opExtrude","CAP_EDGE",EDGE,{"disambiguationData":[OSD([sQuery(id+"F0.wireOp",EDGE,"E66.MirrorCS")])],"isStart":false});Q21=makeQuery(id+"F15.imprint","IMPRINT",FACE,{"disambiguationData":[TD([[makeQuery(id+"F15.imprint","IMPRINT",EDGE,{"derivedFrom":subQ1}),1.0]])]});}
            var Q22;
            {var subQ2=sQuery(id+"F15.wireOp",EDGE,"E214.left");Q22=makeQuery(id+"F15.imprint","IMPRINT",FACE,{"disambiguationData":[TD([[makeQuery(id+"F15.imprint","IMPRINT",EDGE,{"derivedFrom":subQ2}),1.0]])]});}
            var Q23;
            Q23=makeQuery(id+"F5.opExtrude","CAP_FACE",FACE,{"disambiguationData":[OSD([sQuery(id+"F4.wireOp",EDGE,"E154.bottom"),sQuery(id+"F4.wireOp",EDGE,"E154.top"),sQuery(id+"F4.wireOp",EDGE,"E154.left"),sQuery(id+"F4.wireOp",EDGE,"E154.right")])],"isStart":false});
            extrude(context, id + "F16", {"entities" : qUnion([Q0, Q1, Q2, Q3, Q4, Q5, Q6, Q7, Q8, Q9, Q10, Q11, Q12, Q13, Q14, Q15, Q16, Q17, Q18, Q19, Q20, Q21, Q22]), "endBound" : BoundingType.UP_TO_SURFACE, "endBoundEntityFace" : qUnion([Q23]), "depth" : 25 * mm});
        }
        {
            var Q0;
            Q0=makeQuery(id+"F16.opExtrude","SWEPT_BODY",BODY,{"disambiguationData":[OSD([sQuery(id+"F15.wireOp",EDGE,"E214.bottom"),sQuery(id+"F15.wireOp",EDGE,"E214.top"),sQuery(id+"F15.wireOp",EDGE,"E214.left"),sQuery(id+"F15.wireOp",EDGE,"E213.0")])]});
            var Q1;
            Q1=makeQuery(id+"F14.opExtrude","SWEPT_BODY",BODY,{"disambiguationData":[OSD([sQuery(id+"F13.wireOp",EDGE,"E207.6"),sQuery(id+"F13.wireOp",EDGE,"E207.25"),sQuery(id+"F13.wireOp",EDGE,"E207.55"),sQuery(id+"F13.wireOp",EDGE,"E209")])]});
            var Q2;
            Q2=makeQuery(id+"F14.opExtrude","SWEPT_BODY",BODY,{"disambiguationData":[OSD([sQuery(id+"F13.wireOp",EDGE,"E207.20"),sQuery(id+"F13.wireOp",EDGE,"E207.37"),sQuery(id+"F13.wireOp",EDGE,"E207.49"),sQuery(id+"F13.wireOp",EDGE,"E209")])]});
            var Q3;
            Q3=makeQuery(id+"F14.opExtrude","SWEPT_BODY",BODY,{"disambiguationData":[OSD([sQuery(id+"F13.wireOp",EDGE,"E207.10"),sQuery(id+"F13.wireOp",EDGE,"E207.43"),sQuery(id+"F13.wireOp",EDGE,"E207.48"),sQuery(id+"F13.wireOp",EDGE,"E209")])]});
            var Q4;
            Q4=makeQuery(id+"F14.opExtrude","SWEPT_BODY",BODY,{"disambiguationData":[OSD([sQuery(id+"F13.wireOp",EDGE,"E207.17"),sQuery(id+"F13.wireOp",EDGE,"E207.29"),sQuery(id+"F13.wireOp",EDGE,"E207.33"),sQuery(id+"F13.wireOp",EDGE,"E209")])]});
            var Q5;
            Q5=makeQuery(id+"F14.opExtrude","SWEPT_BODY",BODY,{"disambiguationData":[OSD([sQuery(id+"F13.wireOp",EDGE,"E207.31"),sQuery(id+"F13.wireOp",EDGE,"E207.39"),sQuery(id+"F13.wireOp",EDGE,"E207.47"),sQuery(id+"F13.wireOp",EDGE,"E209")])]});
            var Q6;
            Q6=makeQuery(id+"F11.opExtrude","SWEPT_BODY",BODY,{"disambiguationData":[OSD([sQuery(id+"F10.wireOp",EDGE,"E199.104"),sQuery(id+"F10.wireOp",EDGE,"E199.145"),sQuery(id+"F10.wireOp",EDGE,"E199.165"),sQuery(id+"F10.wireOp",EDGE,"E205")])]});
            var Q7;
            Q7=makeQuery(id+"F11.opExtrude","SWEPT_BODY",BODY,{"disambiguationData":[OSD([sQuery(id+"F10.wireOp",EDGE,"E199.116"),sQuery(id+"F10.wireOp",EDGE,"E199.228"),sQuery(id+"F10.wireOp",EDGE,"E199.250"),sQuery(id+"F10.wireOp",EDGE,"E205")])]});
            var Q8;
            Q8=makeQuery(id+"F11.opExtrude","SWEPT_BODY",BODY,{"disambiguationData":[OSD([sQuery(id+"F10.wireOp",EDGE,"E199.164"),sQuery(id+"F10.wireOp",EDGE,"E199.185"),sQuery(id+"F10.wireOp",EDGE,"E199.206"),sQuery(id+"F10.wireOp",EDGE,"E205")])]});
            var Q9;
            Q9=makeQuery(id+"F11.opExtrude","SWEPT_BODY",BODY,{"disambiguationData":[OSD([sQuery(id+"F10.wireOp",EDGE,"E199.110"),sQuery(id+"F10.wireOp",EDGE,"E199.123"),sQuery(id+"F10.wireOp",EDGE,"E199.143"),sQuery(id+"F10.wireOp",EDGE,"E205")])]});
            var Q10;
            Q10=makeQuery(id+"F11.opExtrude","SWEPT_BODY",BODY,{"disambiguationData":[OSD([sQuery(id+"F10.wireOp",EDGE,"E199.205"),sQuery(id+"F10.wireOp",EDGE,"E199.227"),sQuery(id+"F10.wireOp",EDGE,"E199.249"),sQuery(id+"F10.wireOp",EDGE,"E205")])]});
            var Q11;
            Q11=makeQuery(id+"F11.opExtrude","SWEPT_BODY",BODY,{"disambiguationData":[OSD([sQuery(id+"F10.wireOp",EDGE,"E199.186"),sQuery(id+"F10.wireOp",EDGE,"E199.187"),sQuery(id+"F10.wireOp",EDGE,"E199.208"),sQuery(id+"F10.wireOp",EDGE,"E205")])]});
            var Q12;
            Q12=makeQuery(id+"F11.opExtrude","SWEPT_BODY",BODY,{"disambiguationData":[OSD([sQuery(id+"F10.wireOp",EDGE,"E199.144"),sQuery(id+"F10.wireOp",EDGE,"E199.188"),sQuery(id+"F10.wireOp",EDGE,"E199.229"),sQuery(id+"F10.wireOp",EDGE,"E204")])]});
            var Q13;
            Q13=makeQuery(id+"F11.opExtrude","SWEPT_BODY",BODY,{"disambiguationData":[OSD([sQuery(id+"F10.wireOp",EDGE,"E199.93"),sQuery(id+"F10.wireOp",EDGE,"E199.146"),sQuery(id+"F10.wireOp",EDGE,"E199.230"),sQuery(id+"F10.wireOp",EDGE,"E203")])]});
            var Q14;
            Q14=makeQuery(id+"F11.opExtrude","SWEPT_BODY",BODY,{"disambiguationData":[OSD([sQuery(id+"F10.wireOp",EDGE,"E199.107"),sQuery(id+"F10.wireOp",EDGE,"E199.166"),sQuery(id+"F10.wireOp",EDGE,"E199.252"),sQuery(id+"F10.wireOp",EDGE,"E202")])]});
            var Q15;
            Q15=makeQuery(id+"F11.opExtrude","SWEPT_BODY",BODY,{"disambiguationData":[OSD([sQuery(id+"F10.wireOp",EDGE,"E199.108"),sQuery(id+"F10.wireOp",EDGE,"E199.167"),sQuery(id+"F10.wireOp",EDGE,"E199.207"),sQuery(id+"F10.wireOp",EDGE,"E201")])]});
            var Q16;
            Q16=makeQuery(id+"F11.opExtrude","SWEPT_BODY",BODY,{"disambiguationData":[OSD([sQuery(id+"F10.wireOp",EDGE,"E199.121"),sQuery(id+"F10.wireOp",EDGE,"E199.209"),sQuery(id+"F10.wireOp",EDGE,"E199.251"),sQuery(id+"F10.wireOp",EDGE,"E200")])]});
            var Q17;
            Q17=makeQuery(id+"F12.opExtrude","SWEPT_BODY",BODY,{"disambiguationData":[OSD([sQuery(id+"F7.wireOp",EDGE,"E181.MirrorCS"),sQuery(id+"F7.wireOp",EDGE,"E184.MirrorCS"),sQuery(id+"F7.wireOp",EDGE,"E193.MirrorCS"),sQuery(id+"F7.wireOp",EDGE,"E194.MirrorCS")])]});
            var Q18;
            Q18=makeQuery(id+"F12.opExtrude","SWEPT_BODY",BODY,{"disambiguationData":[OSD([sQuery(id+"F7.wireOp",EDGE,"E179.MirrorCS"),sQuery(id+"F7.wireOp",EDGE,"E182.MirrorCS"),sQuery(id+"F7.wireOp",EDGE,"E190.MirrorCS"),sQuery(id+"F7.wireOp",EDGE,"E192.MirrorCS")])]});
            var Q19;
            Q19=makeQuery(id+"F12.opExtrude","SWEPT_BODY",BODY,{"disambiguationData":[OSD([sQuery(id+"F7.wireOp",EDGE,"E175.MirrorCS"),sQuery(id+"F7.wireOp",EDGE,"E174.MirrorCS"),sQuery(id+"F7.wireOp",EDGE,"E176.MirrorCS"),sQuery(id+"F7.wireOp",EDGE,"E188.MirrorCS")])]});
            var Q20;
            Q20=makeQuery(id+"F12.opExtrude","SWEPT_BODY",BODY,{"disambiguationData":[OSD([sQuery(id+"F7.wireOp",EDGE,"E180.MirrorCS"),sQuery(id+"F7.wireOp",EDGE,"E183.MirrorCS"),sQuery(id+"F7.wireOp",EDGE,"E189.MirrorCS"),sQuery(id+"F7.wireOp",EDGE,"E191.MirrorCS")])]});
            var Q21;
            Q21=makeQuery(id+"F12.opExtrude","SWEPT_BODY",BODY,{"disambiguationData":[OSD([sQuery(id+"F7.wireOp",EDGE,"E185.MirrorCS"),sQuery(id+"F7.wireOp",EDGE,"E186.MirrorCS"),sQuery(id+"F7.wireOp",EDGE,"E195.MirrorCS"),sQuery(id+"F7.wireOp",EDGE,"E196.MirrorCS")])]});
            booleanBodies(context, id + "F17", {"operationType" : BooleanOperationType.UNION, "tools" : qUnion([Q0, Q1, Q2, Q3, Q4, Q5, Q6, Q7, Q8, Q9, Q10, Q11, Q12, Q13, Q14, Q15, Q16, Q17, Q18, Q19, Q20, Q21])});
        }
        {
            var Q0;
            Q0=makeQuery(id+"F11.opExtrude","SWEPT_BODY",BODY,{"disambiguationData":[OSD([sQuery(id+"F10.wireOp",EDGE,"E199.91"),sQuery(id+"F10.wireOp",EDGE,"E199.234"),sQuery(id+"F10.wireOp",EDGE,"E199.256"),sQuery(id+"F10.wireOp",EDGE,"E206")])]});
            var Q1;
            Q1=makeQuery(id+"F11.opExtrude","SWEPT_BODY",BODY,{"disambiguationData":[OSD([sQuery(id+"F10.wireOp",EDGE,"E199.94"),sQuery(id+"F10.wireOp",EDGE,"E199.136"),sQuery(id+"F10.wireOp",EDGE,"E199.255"),sQuery(id+"F10.wireOp",EDGE,"E206")])]});
            var Q2;
            Q2=makeQuery(id+"F11.opExtrude","SWEPT_BODY",BODY,{"disambiguationData":[OSD([sQuery(id+"F10.wireOp",EDGE,"E199.98"),sQuery(id+"F10.wireOp",EDGE,"E199.153"),sQuery(id+"F10.wireOp",EDGE,"E199.212"),sQuery(id+"F10.wireOp",EDGE,"E206")])]});
            var Q3;
            Q3=makeQuery(id+"F11.opExtrude","SWEPT_BODY",BODY,{"disambiguationData":[OSD([sQuery(id+"F10.wireOp",EDGE,"E199.106"),sQuery(id+"F10.wireOp",EDGE,"E199.125"),sQuery(id+"F10.wireOp",EDGE,"E199.172"),sQuery(id+"F10.wireOp",EDGE,"E206")])]});
            var Q4;
            Q4=makeQuery(id+"F11.opExtrude","SWEPT_BODY",BODY,{"disambiguationData":[OSD([sQuery(id+"F10.wireOp",EDGE,"E199.113"),sQuery(id+"F10.wireOp",EDGE,"E199.192"),sQuery(id+"F10.wireOp",EDGE,"E199.235"),sQuery(id+"F10.wireOp",EDGE,"E206")])]});
            var Q5;
            Q5=makeQuery(id+"F11.opExtrude","SWEPT_BODY",BODY,{"disambiguationData":[OSD([sQuery(id+"F10.wireOp",EDGE,"E199.135"),sQuery(id+"F10.wireOp",EDGE,"E199.211"),sQuery(id+"F10.wireOp",EDGE,"E199.257"),sQuery(id+"F10.wireOp",EDGE,"E206")])]});
            var Q6;
            Q6=makeQuery(id+"F11.opExtrude","SWEPT_BODY",BODY,{"disambiguationData":[OSD([sQuery(id+"F10.wireOp",EDGE,"E199.148"),sQuery(id+"F10.wireOp",EDGE,"E199.169"),sQuery(id+"F10.wireOp",EDGE,"E199.190"),sQuery(id+"F10.wireOp",EDGE,"E206")])]});
            var Q7;
            Q7=makeQuery(id+"F11.opExtrude","SWEPT_BODY",BODY,{"disambiguationData":[OSD([sQuery(id+"F10.wireOp",EDGE,"E199.149"),sQuery(id+"F10.wireOp",EDGE,"E199.150"),sQuery(id+"F10.wireOp",EDGE,"E199.237"),sQuery(id+"F10.wireOp",EDGE,"E206")])]});
            var Q8;
            Q8=makeQuery(id+"F11.opExtrude","SWEPT_BODY",BODY,{"disambiguationData":[OSD([sQuery(id+"F10.wireOp",EDGE,"E199.152"),sQuery(id+"F10.wireOp",EDGE,"E199.170"),sQuery(id+"F10.wireOp",EDGE,"E199.191"),sQuery(id+"F10.wireOp",EDGE,"E206")])]});
            var Q9;
            Q9=makeQuery(id+"F11.opExtrude","SWEPT_BODY",BODY,{"disambiguationData":[OSD([sQuery(id+"F10.wireOp",EDGE,"E199.171"),sQuery(id+"F10.wireOp",EDGE,"E199.174"),sQuery(id+"F10.wireOp",EDGE,"E199.233"),sQuery(id+"F10.wireOp",EDGE,"E206")])]});
            var Q10;
            Q10=makeQuery(id+"F11.opExtrude","SWEPT_BODY",BODY,{"disambiguationData":[OSD([sQuery(id+"F10.wireOp",EDGE,"E199.193"),sQuery(id+"F10.wireOp",EDGE,"E199.213"),sQuery(id+"F10.wireOp",EDGE,"E199.232"),sQuery(id+"F10.wireOp",EDGE,"E206")])]});
            var Q11;
            Q11=makeQuery(id+"F12.opExtrude","SWEPT_BODY",BODY,{"disambiguationData":[OSD([sQuery(id+"F7.wireOp",EDGE,"E157"),sQuery(id+"F7.wireOp",EDGE,"E159"),sQuery(id+"F7.wireOp",EDGE,"E158.MirrorCS"),sQuery(id+"F7.wireOp",EDGE,"E171")])]});
            var Q12;
            Q12=makeQuery(id+"F12.opExtrude","SWEPT_BODY",BODY,{"disambiguationData":[OSD([sQuery(id+"F7.wireOp",EDGE,"E160.0.1.0"),sQuery(id+"F7.wireOp",EDGE,"E160.0.1.1"),sQuery(id+"F7.wireOp",EDGE,"E160.0.1.2"),sQuery(id+"F7.wireOp",EDGE,"E170")])]});
            var Q13;
            Q13=makeQuery(id+"F12.opExtrude","SWEPT_BODY",BODY,{"disambiguationData":[OSD([sQuery(id+"F7.wireOp",EDGE,"E160.0.2.0"),sQuery(id+"F7.wireOp",EDGE,"E160.0.2.1"),sQuery(id+"F7.wireOp",EDGE,"E160.0.2.2"),sQuery(id+"F7.wireOp",EDGE,"E169")])]});
            var Q14;
            Q14=makeQuery(id+"F12.opExtrude","SWEPT_BODY",BODY,{"disambiguationData":[OSD([sQuery(id+"F7.wireOp",EDGE,"E161.MirrorCS"),sQuery(id+"F7.wireOp",EDGE,"E164.MirrorCS"),sQuery(id+"F7.wireOp",EDGE,"E165.MirrorCS"),sQuery(id+"F7.wireOp",EDGE,"E173")])]});
            var Q15;
            Q15=makeQuery(id+"F12.opExtrude","SWEPT_BODY",BODY,{"disambiguationData":[OSD([sQuery(id+"F7.wireOp",EDGE,"E163.MirrorCS"),sQuery(id+"F7.wireOp",EDGE,"E166.MirrorCS"),sQuery(id+"F7.wireOp",EDGE,"E168.MirrorCS"),sQuery(id+"F7.wireOp",EDGE,"E172")])]});
            var Q16;
            Q16=makeQuery(id+"F14.opExtrude","SWEPT_BODY",BODY,{"disambiguationData":[OSD([sQuery(id+"F13.wireOp",EDGE,"E208.1"),sQuery(id+"F13.wireOp",EDGE,"E208.5"),sQuery(id+"F13.wireOp",EDGE,"E208.37"),sQuery(id+"F13.wireOp",EDGE,"E210")])]});
            var Q17;
            Q17=makeQuery(id+"F14.opExtrude","SWEPT_BODY",BODY,{"disambiguationData":[OSD([sQuery(id+"F13.wireOp",EDGE,"E208.12"),sQuery(id+"F13.wireOp",EDGE,"E208.33"),sQuery(id+"F13.wireOp",EDGE,"E208.42"),sQuery(id+"F13.wireOp",EDGE,"E210")])]});
            var Q18;
            Q18=makeQuery(id+"F14.opExtrude","SWEPT_BODY",BODY,{"disambiguationData":[OSD([sQuery(id+"F13.wireOp",EDGE,"E208.15"),sQuery(id+"F13.wireOp",EDGE,"E208.38"),sQuery(id+"F13.wireOp",EDGE,"E208.51"),sQuery(id+"F13.wireOp",EDGE,"E210")])]});
            var Q19;
            Q19=makeQuery(id+"F14.opExtrude","SWEPT_BODY",BODY,{"disambiguationData":[OSD([sQuery(id+"F13.wireOp",EDGE,"E208.20"),sQuery(id+"F13.wireOp",EDGE,"E208.22"),sQuery(id+"F13.wireOp",EDGE,"E208.45"),sQuery(id+"F13.wireOp",EDGE,"E210")])]});
            var Q20;
            Q20=makeQuery(id+"F14.opExtrude","SWEPT_BODY",BODY,{"disambiguationData":[OSD([sQuery(id+"F13.wireOp",EDGE,"E208.29"),sQuery(id+"F13.wireOp",EDGE,"E208.39"),sQuery(id+"F13.wireOp",EDGE,"E208.53"),sQuery(id+"F13.wireOp",EDGE,"E210")])]});
            deleteBodies(context, id + "F18", {"entities" : qUnion([Q0, Q1, Q2, Q3, Q4, Q5, Q6, Q7, Q8, Q9, Q10, Q11, Q12, Q13, Q14, Q15, Q16, Q17, Q18, Q19, Q20])});
        }
        {
            var Q0;
            Q0=makeQuery(id+"F16.opExtrude","SWEPT_BODY",BODY,{"disambiguationData":[OSD([sQuery(id+"F15.wireOp",EDGE,"E214.bottom"),sQuery(id+"F15.wireOp",EDGE,"E214.top"),sQuery(id+"F15.wireOp",EDGE,"E214.left"),sQuery(id+"F15.wireOp",EDGE,"E213.0")])]});
            var Q1;
            Q1=qCreatedBy(makeId("Front.planeOp"),FACE);
            mirror(context, id + "F19", {"entities" : qUnion([Q0]), "mirrorPlane" : qUnion([Q1])});
        }
        {
            var Q0;
            Q0=makeQuery(id+"F5.opExtrude","CAP_FACE",FACE,{"disambiguationData":[OSD([sQuery(id+"F4.wireOp",EDGE,"E154.bottom"),sQuery(id+"F4.wireOp",EDGE,"E154.top"),sQuery(id+"F4.wireOp",EDGE,"E154.left"),sQuery(id+"F4.wireOp",EDGE,"E154.right")])],"isStart":false});
            var sketch = newSketch(context, id + "F20", { "sketchPlane" : qUnion([Q0])});
            skLineSegment(sketch, "E219.0.1", {"start": v(-146, 100) * mm, "end": v(-150, 100) * mm});
            skLineSegment(sketch, "E219.0.2", {"start": v(-150, 100) * mm, "end": v(-150, -100) * mm});
            skLineSegment(sketch, "E219.0.3", {"start": v(-150, -100) * mm, "end": v(-146, -100) * mm});
            skLineSegment(sketch, "E220.0.0", {"start": v(146, 100) * mm, "end": v(-146, 100) * mm});
            skLineSegment(sketch, "E221.0.1", {"start": v(146, -100) * mm, "end": v(150, -100) * mm});
            skLineSegment(sketch, "E221.0.2", {"start": v(150, -100) * mm, "end": v(150, 100) * mm});
            skLineSegment(sketch, "E221.0.3", {"start": v(150, 100) * mm, "end": v(146, 100) * mm});
            skLineSegment(sketch, "E222.0.0", {"start": v(-146, -100) * mm, "end": v(146, -100) * mm});
            skLineSegment(sketch, "E223.0", {"start": v(146, 96) * mm, "end": v(-146, 96) * mm});
            skLineSegment(sketch, "E223.1", {"start": v(146, -96) * mm, "end": v(146, 96) * mm});
            skLineSegment(sketch, "E223.2", {"start": v(-146, -96) * mm, "end": v(146, -96) * mm});
            skLineSegment(sketch, "E223.3", {"start": v(-146, 96) * mm, "end": v(-146, -96) * mm});
            skLineSegment(sketch, "E224.0", {"start": v(142, 92) * mm, "end": v(-142, 92) * mm});
            skLineSegment(sketch, "E224.1", {"start": v(142, -92) * mm, "end": v(142, 92) * mm});
            skLineSegment(sketch, "E224.2", {"start": v(-142, -92) * mm, "end": v(142, -92) * mm});
            skLineSegment(sketch, "E224.3", {"start": v(-142, 92) * mm, "end": v(-142, -92) * mm});
            skLineSegment(sketch, "E225", {"start": v(142, -92) * mm, "end": v(140.59, -90.59) * mm});
            skCircle(sketch, "E226", {"center": v(140.59, -90.59) * mm, "radius": 0.5 * mm});
            skSolve(sketch);
        }
        {
            var Q0;
            Q0 = qSketchRegion(id + "F20", true);
            var Q1;
            Q1=makeQuery(id+"F20.imprint","IMPRINT",FACE,{"disambiguationData":[TD([[makeQuery(id+"F20.imprint","IMPRINT",EDGE,{"derivedFrom":sQuery(id+"F20.wireOp",EDGE,"E224.0")}),1.0]])]});
            var Q2;
            Q2=makeQuery(id+"F20.imprint","IMPRINT",FACE,{"disambiguationData":[TD([[makeQuery(id+"F20.imprint","IMPRINT",EDGE,{"derivedFrom":sQuery(id+"F20.wireOp",EDGE,"E223.0")}),1.0]])]});
            extrude(context, id + "F21", {"entities" : qUnion([Q0, Q1, Q2]), "depth" : 4 * mm});
        }
        {
            var Q0;
            Q0=makeQuery(id+"F20.imprint","IMPRINT",FACE,{"disambiguationData":[TD([[makeQuery(id+"F20.imprint","IMPRINT",EDGE,{"derivedFrom":sQuery(id+"F20.wireOp",EDGE,"E223.0")}),1.0]])]});
            extrude(context, id + "F22", {"entities" : qUnion([Q0]), "operationType" : NewBodyOperationType.ADD, "oppositeDirection" : true, "depth" : 8 * mm});
        }
        {
            var Q0;
            {var subQ0=sQuery(id+"F13.wireOp",EDGE,"E209");var subQ15=sQuery(id+"F10.wireOp",EDGE,"E205");Q0=makeQuery(id+"F19.opPattern","COPY",FACE,{"derivedFrom":makeQuery(id+"F17.opBoolean","MERGE",FACE,{"derivedFrom":[makeQuery(id+"F11.opExtrude","SWEPT_FACE",FACE,{"disambiguationData":[OSD([sQuery(id+"F10.wireOp",EDGE,"E200")])]}),makeQuery(id+"F11.opExtrude","SWEPT_FACE",FACE,{"disambiguationData":[OSD([sQuery(id+"F10.wireOp",EDGE,"E201")])]}),makeQuery(id+"F11.opExtrude","SWEPT_FACE",FACE,{"disambiguationData":[OSD([sQuery(id+"F10.wireOp",EDGE,"E202")])]}),makeQuery(id+"F11.opExtrude","SWEPT_FACE",FACE,{"disambiguationData":[OSD([sQuery(id+"F10.wireOp",EDGE,"E203")])]}),makeQuery(id+"F11.opExtrude","SWEPT_FACE",FACE,{"disambiguationData":[OSD([sQuery(id+"F10.wireOp",EDGE,"E204")])]}),makeQuery(id+"F11.opExtrude","SWEPT_FACE",FACE,{"disambiguationData":[OSD([subQ15]),TDD([makeQuery(id+"F10.imprint","IMPRINT",EDGE,{"disambiguationData":[TD([[makeQuery(id+"F10.imprint","INTERSECT",VERTEX,{"derivedFrom":[sQuery(id+"F10.wireOp",EDGE,"E199.208"),subQ15]}),1.0]])],"derivedFrom":subQ15})])]}),makeQuery(id+"F11.opExtrude","SWEPT_FACE",FACE,{"disambiguationData":[OSD([subQ15]),TDD([makeQuery(id+"F10.imprint","IMPRINT",EDGE,{"disambiguationData":[TD([[makeQuery(id+"F10.imprint","INTERSECT",VERTEX,{"derivedFrom":[sQuery(id+"F10.wireOp",EDGE,"E199.205"),subQ15]}),-1.0]])],"derivedFrom":subQ15})])]}),makeQuery(id+"F11.opExtrude","SWEPT_FACE",FACE,{"disambiguationData":[OSD([subQ15]),TDD([makeQuery(id+"F10.imprint","IMPRINT",EDGE,{"disambiguationData":[TD([[makeQuery(id+"F10.imprint","INTERSECT",VERTEX,{"derivedFrom":[sQuery(id+"F10.wireOp",EDGE,"E199.110"),subQ15]}),-1.0]])],"derivedFrom":subQ15})])]}),makeQuery(id+"F11.opExtrude","SWEPT_FACE",FACE,{"disambiguationData":[OSD([subQ15]),TDD([makeQuery(id+"F10.imprint","IMPRINT",EDGE,{"disambiguationData":[TD([[makeQuery(id+"F10.imprint","INTERSECT",VERTEX,{"derivedFrom":[sQuery(id+"F10.wireOp",EDGE,"E199.164"),subQ15]}),-1.0]])],"derivedFrom":subQ15})])]}),makeQuery(id+"F11.opExtrude","SWEPT_FACE",FACE,{"disambiguationData":[OSD([subQ15]),TDD([makeQuery(id+"F10.imprint","IMPRINT",EDGE,{"disambiguationData":[TD([[makeQuery(id+"F10.imprint","INTERSECT",VERTEX,{"derivedFrom":[sQuery(id+"F10.wireOp",EDGE,"E199.228"),subQ15]}),-1.0]])],"derivedFrom":subQ15})])]}),makeQuery(id+"F11.opExtrude","SWEPT_FACE",FACE,{"disambiguationData":[OSD([subQ15]),TDD([makeQuery(id+"F10.imprint","IMPRINT",EDGE,{"disambiguationData":[TD([[makeQuery(id+"F10.imprint","INTERSECT",VERTEX,{"derivedFrom":[sQuery(id+"F10.wireOp",EDGE,"E199.104"),subQ15]}),-1.0]])],"derivedFrom":subQ15})])]}),makeQuery(id+"F12.opExtrude","SWEPT_FACE",FACE,{"disambiguationData":[OSD([sQuery(id+"F7.wireOp",EDGE,"E188.MirrorCS")])]}),makeQuery(id+"F12.opExtrude","SWEPT_FACE",FACE,{"disambiguationData":[OSD([sQuery(id+"F7.wireOp",EDGE,"E189.MirrorCS")])]}),makeQuery(id+"F12.opExtrude","SWEPT_FACE",FACE,{"disambiguationData":[OSD([sQuery(id+"F7.wireOp",EDGE,"E190.MirrorCS")])]}),makeQuery(id+"F12.opExtrude","SWEPT_FACE",FACE,{"disambiguationData":[OSD([sQuery(id+"F7.wireOp",EDGE,"E193.MirrorCS")])]}),makeQuery(id+"F12.opExtrude","SWEPT_FACE",FACE,{"disambiguationData":[OSD([sQuery(id+"F7.wireOp",EDGE,"E196.MirrorCS")])]}),makeQuery(id+"F14.opExtrude","SWEPT_FACE",FACE,{"disambiguationData":[OSD([subQ0]),TDD([makeQuery(id+"F13.imprint","IMPRINT",EDGE,{"disambiguationData":[TD([[makeQuery(id+"F13.imprint","INTERSECT",VERTEX,{"derivedFrom":[sQuery(id+"F13.wireOp",EDGE,"E207.6"),subQ0]}),1.0]])],"derivedFrom":subQ0})])]}),makeQuery(id+"F14.opExtrude","SWEPT_FACE",FACE,{"disambiguationData":[OSD([subQ0]),TDD([makeQuery(id+"F13.imprint","IMPRINT",EDGE,{"disambiguationData":[TD([[makeQuery(id+"F13.imprint","INTERSECT",VERTEX,{"derivedFrom":[sQuery(id+"F13.wireOp",EDGE,"E207.37"),subQ0]}),-1.0]])],"derivedFrom":subQ0})])]}),makeQuery(id+"F14.opExtrude","SWEPT_FACE",FACE,{"disambiguationData":[OSD([subQ0]),TDD([makeQuery(id+"F13.imprint","IMPRINT",EDGE,{"disambiguationData":[TD([[makeQuery(id+"F13.imprint","INTERSECT",VERTEX,{"derivedFrom":[sQuery(id+"F13.wireOp",EDGE,"E207.10"),subQ0]}),1.0]])],"derivedFrom":subQ0})])]}),makeQuery(id+"F14.opExtrude","SWEPT_FACE",FACE,{"disambiguationData":[OSD([subQ0]),TDD([makeQuery(id+"F13.imprint","IMPRINT",EDGE,{"disambiguationData":[TD([[makeQuery(id+"F13.imprint","INTERSECT",VERTEX,{"derivedFrom":[sQuery(id+"F13.wireOp",EDGE,"E207.17"),subQ0]}),1.0]])],"derivedFrom":subQ0})])]}),makeQuery(id+"F14.opExtrude","SWEPT_FACE",FACE,{"disambiguationData":[OSD([subQ0]),TDD([makeQuery(id+"F13.imprint","IMPRINT",EDGE,{"disambiguationData":[TD([[makeQuery(id+"F13.imprint","INTERSECT",VERTEX,{"derivedFrom":[sQuery(id+"F13.wireOp",EDGE,"E207.31"),subQ0]}),-1.0]])],"derivedFrom":subQ0})])]}),makeQuery(id+"F16.opExtrude","SWEPT_FACE",FACE,{"disambiguationData":[OSD([sQuery(id+"F15.wireOp",EDGE,"E214.bottom")])]})]}),"instanceName":"1"});}
            var sketch = newSketch(context, id + "F23", { "sketchPlane" : qUnion([Q0])});
            skLineSegment(sketch, "E227.0", {"start": v(150, 79) * mm, "end": v(150, 69) * mm});
            skLineSegment(sketch, "E228.bottom", {"start": v(141.03, 76.35) * mm, "end": v(144.1, 76.35) * mm});
            skLineSegment(sketch, "E228.top", {"start": v(141.03, 70.14) * mm, "end": v(144.1, 70.14) * mm});
            skLineSegment(sketch, "E228.left", {"start": v(141.03, 76.35) * mm, "end": v(141.03, 70.14) * mm});
            skLineSegment(sketch, "E228.right", {"start": v(144.1, 76.35) * mm, "end": v(144.1, 70.14) * mm});
            skLineSegment(sketch, "E229.bottom", {"start": v(142.52, 75.76) * mm, "end": v(144.02, 75.76) * mm});
            skLineSegment(sketch, "E229.top", {"start": v(142.52, 71.76) * mm, "end": v(144.02, 71.76) * mm});
            skLineSegment(sketch, "E229.left", {"start": v(142.52, 75.76) * mm, "end": v(142.52, 71.76) * mm});
            skLineSegment(sketch, "E229.right", {"start": v(144.02, 75.76) * mm, "end": v(144.02, 71.76) * mm});
            skSolve(sketch);
        }
        {
            var Q0;
            Q0 = qSketchRegion(id + "F23", true);
            var Q1;
            Q1=makeQuery(id+"F23.imprint","IMPRINT",FACE,{"disambiguationData":[TD([[makeQuery(id+"F23.imprint","IMPRINT",EDGE,{"derivedFrom":sQuery(id+"F23.wireOp",EDGE,"E229.bottom")}),-1.0]])]});
            var Q2;
            Q2=sQuery(id+"F23.wireOp",EDGE,"E227.0");
            revolve(context, id + "F24", {"operationType" : NewBodyOperationType.REMOVE, "entities" : qUnion([Q0, Q1]), "axis" : qUnion([Q2]), "revolveType" : RevolveType.FULL, "oppositeDirection" : true});
        }
        {
            var Q0;
            Q0=makeQuery(id+"F24.boolean.opBoolean","COPY",FACE,{"disambiguationData":[TD([makeQuery(id+"F19.opPattern","COPY",FACE,{"derivedFrom":makeQuery(id+"F17.opBoolean","MERGE",FACE,{"derivedFrom":[makeQuery(id+"F11.opExtrude","SWEPT_FACE",FACE,{"disambiguationData":[OSD([sQuery(id+"F10.wireOp",EDGE,"E199.107")])]}),makeQuery(id+"F11.opExtrude","SWEPT_FACE",FACE,{"disambiguationData":[OSD([sQuery(id+"F10.wireOp",EDGE,"E199.116")])]}),makeQuery(id+"F11.opExtrude","SWEPT_FACE",FACE,{"disambiguationData":[OSD([sQuery(id+"F10.wireOp",EDGE,"E199.143")])]}),makeQuery(id+"F11.opExtrude","SWEPT_FACE",FACE,{"disambiguationData":[OSD([sQuery(id+"F10.wireOp",EDGE,"E199.146")])]}),makeQuery(id+"F11.opExtrude","SWEPT_FACE",FACE,{"disambiguationData":[OSD([sQuery(id+"F10.wireOp",EDGE,"E199.165")])]}),makeQuery(id+"F11.opExtrude","SWEPT_FACE",FACE,{"disambiguationData":[OSD([sQuery(id+"F10.wireOp",EDGE,"E199.167")])]}),makeQuery(id+"F11.opExtrude","SWEPT_FACE",FACE,{"disambiguationData":[OSD([sQuery(id+"F10.wireOp",EDGE,"E199.186")])]}),makeQuery(id+"F11.opExtrude","SWEPT_FACE",FACE,{"disambiguationData":[OSD([sQuery(id+"F10.wireOp",EDGE,"E199.188")])]}),makeQuery(id+"F11.opExtrude","SWEPT_FACE",FACE,{"disambiguationData":[OSD([sQuery(id+"F10.wireOp",EDGE,"E199.206")])]}),makeQuery(id+"F11.opExtrude","SWEPT_FACE",FACE,{"disambiguationData":[OSD([sQuery(id+"F10.wireOp",EDGE,"E199.209")])]}),makeQuery(id+"F11.opExtrude","SWEPT_FACE",FACE,{"disambiguationData":[OSD([sQuery(id+"F10.wireOp",EDGE,"E199.249")])]}),makeQuery(id+"F12.opExtrude","SWEPT_FACE",FACE,{"disambiguationData":[OSD([sQuery(id+"F7.wireOp",EDGE,"E175.MirrorCS")])]}),makeQuery(id+"F12.opExtrude","SWEPT_FACE",FACE,{"disambiguationData":[OSD([sQuery(id+"F7.wireOp",EDGE,"E191.MirrorCS")])]}),makeQuery(id+"F12.opExtrude","SWEPT_FACE",FACE,{"disambiguationData":[OSD([sQuery(id+"F7.wireOp",EDGE,"E192.MirrorCS")])]}),makeQuery(id+"F12.opExtrude","SWEPT_FACE",FACE,{"disambiguationData":[OSD([sQuery(id+"F7.wireOp",EDGE,"E194.MirrorCS")])]}),makeQuery(id+"F12.opExtrude","SWEPT_FACE",FACE,{"disambiguationData":[OSD([sQuery(id+"F7.wireOp",EDGE,"E195.MirrorCS")])]}),makeQuery(id+"F14.opExtrude","SWEPT_FACE",FACE,{"disambiguationData":[OSD([sQuery(id+"F13.wireOp",EDGE,"E207.29")])]}),makeQuery(id+"F14.opExtrude","SWEPT_FACE",FACE,{"disambiguationData":[OSD([sQuery(id+"F13.wireOp",EDGE,"E207.47")])]}),makeQuery(id+"F14.opExtrude","SWEPT_FACE",FACE,{"disambiguationData":[OSD([sQuery(id+"F13.wireOp",EDGE,"E207.48")])]}),makeQuery(id+"F14.opExtrude","SWEPT_FACE",FACE,{"disambiguationData":[OSD([sQuery(id+"F13.wireOp",EDGE,"E207.49")])]}),makeQuery(id+"F14.opExtrude","SWEPT_FACE",FACE,{"disambiguationData":[OSD([sQuery(id+"F13.wireOp",EDGE,"E207.55")])]}),makeQuery(id+"F16.opExtrude","SWEPT_FACE",FACE,{"disambiguationData":[OSD([sQuery(id+"F15.wireOp",EDGE,"E214.top")])]})]}),"instanceName":"1"})])],"derivedFrom":makeQuery(id+"F24.opRevolve","SWEPT_FACE",FACE,{"disambiguationData":[OSD([sQuery(id+"F23.wireOp",EDGE,"E228.top")])]})});
            var sketch = newSketch(context, id + "F25", { "sketchPlane" : qUnion([Q0])});
            skArc(sketch, "E230", {"start": v(150.57, -92.87) * mm, "mid": v(145.04, -94.85) * mm, "end": v(142.86, -100.3) * mm});
            skArc(sketch, "E231", {"start": v(142.86, -100.3) * mm, "mid": v(151.1, -101.14) * mm, "end": v(150.57, -92.87) * mm});
            skSolve(sketch);
        }
        {
            var Q0;
            Q0=makeQuery(id+"F23.imprint","IMPRINT",FACE,{"disambiguationData":[TD([[makeQuery(id+"F23.imprint","IMPRINT",EDGE,{"derivedFrom":sQuery(id+"F23.wireOp",EDGE,"E229.bottom")}),-1.0]])]});
            var Q1;
            Q1=sQuery(id+"F25.wireOp",EDGE,"E231");
            var Q2;
            Q2=sQuery(id+"F25.wireOp",EDGE,"E230");
            sweep(context, id + "F26", {"profiles" : qUnion([Q0]), "path" : qUnion([Q1, Q2])});
        }
        {
            var Q0;
            Q0=makeQuery(id+"F26.opSweep","MID_CAP_EDGE",EDGE,{"disambiguationData":[OSD([sQuery(id+"F23.wireOp",EDGE,"E229.left"),sQuery(id+"F25.wireOp",VERTEX,"E230.start")])],"capPos":1.0});
            var Q1;
            Q1=makeQuery(id+"F26.opSweep","CAP_EDGE",EDGE,{"disambiguationData":[OSD([sQuery(id+"F23.wireOp",EDGE,"E229.left"),sQuery(id+"F25.wireOp",VERTEX,"E230.end")])],"isStart":true});
            fillet(context, id + "F27", {"entities" : qUnion([Q0, Q1]), "radius" : 2 * mm, "tangentPropagation" : true, "allowEdgeOverflow" : false});
        }
    });
